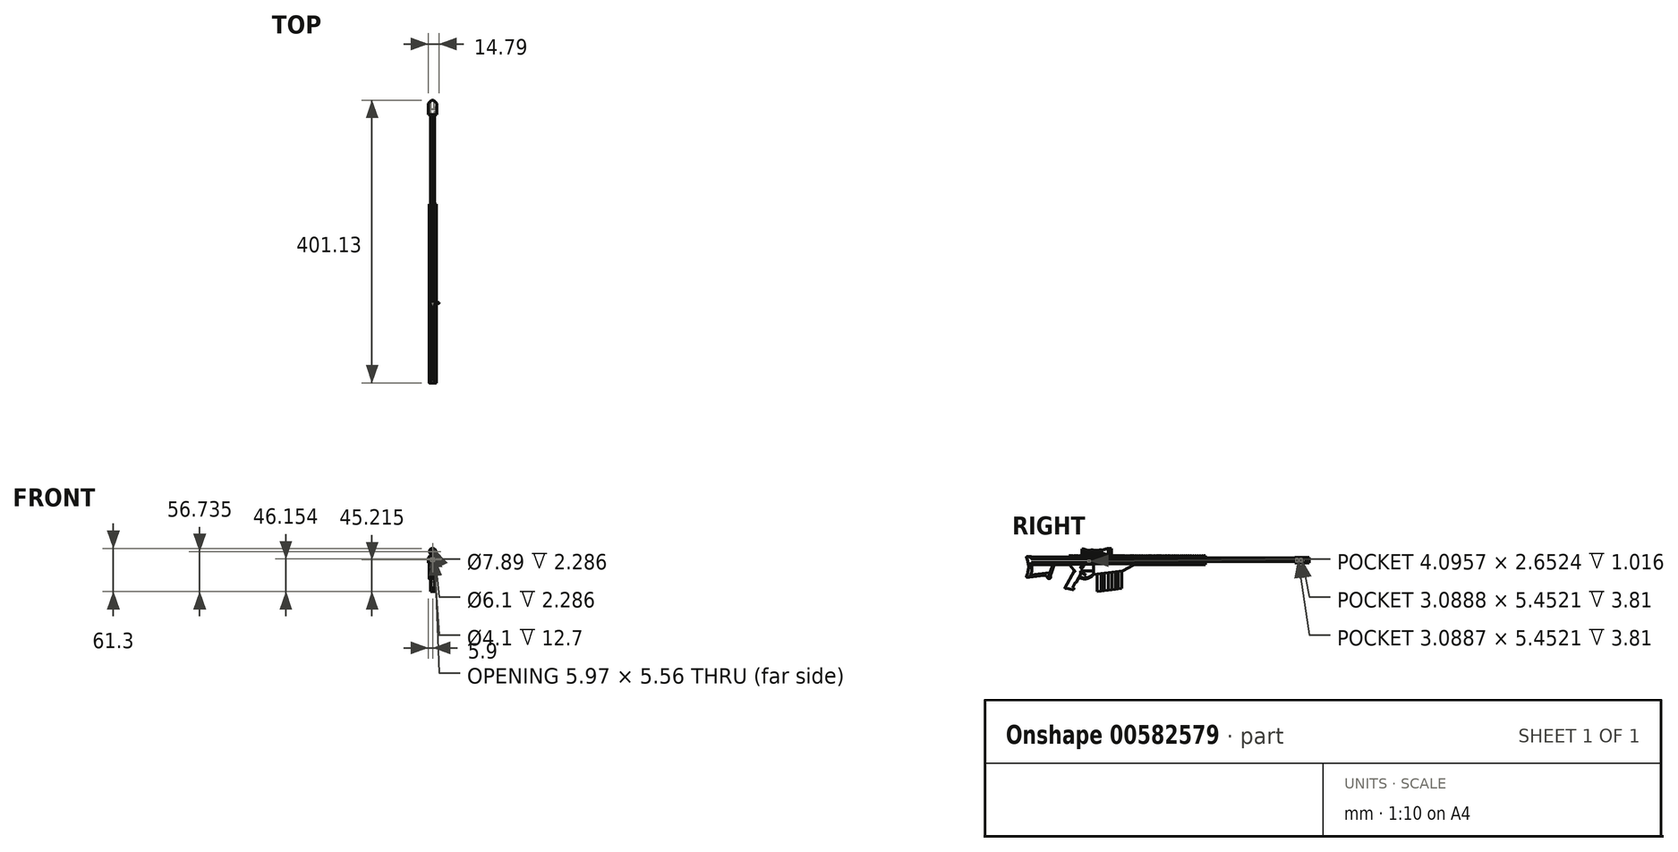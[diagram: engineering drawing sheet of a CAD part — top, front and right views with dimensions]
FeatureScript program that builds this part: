
annotation { "Feature Type Name" : "Feature", "Feature Type Description" : "" }
export const myFeature = defineFeature(function(context is Context, id is Id, definition is map)
    precondition{}
    {
        {
            var Q0;
            Q0=qCreatedBy(makeId("Right.planeOp"),FACE);
            var sketch = newSketch(context, id + "F0", { "sketchPlane" : qUnion([Q0])});
            skArc(sketch, "E0", {"start": v(-85.12, 1.27) * mm, "mid": v(-82.19, 14.92) * mm, "end": v(-85.15, 28.57) * mm});
            skLineSegment(sketch, "E1", {"start": v(-84.31, 0.17) * mm, "end": v(-60.4, 3.1) * mm});
            skArc(sketch, "E2", {"start": v(-55.44, 0) * mm, "mid": v(-57.37, 2.43) * mm, "end": v(-60.4, 3.1) * mm});
            skArc(sketch, "E3", {"start": v(-55.44, 0) * mm, "mid": v(-51.74, -1.3) * mm, "end": v(-51.3, 2.6) * mm});
            skLineSegment(sketch, "E4", {"start": v(-51.3, 2.6) * mm, "end": v(-45.62, 17.62) * mm});
            skArc(sketch, "E5", {"start": v(-80.7, 0.62) * mm, "mid": v(-77.5, 9.24) * mm, "end": v(-78, 18.43) * mm});
            skLineSegment(sketch, "E6", {"start": v(-47.77, 17.62) * mm, "end": v(-51.9, 6.68) * mm});
            skLineSegment(sketch, "E7", {"start": v(-51.9, 6.68) * mm, "end": v(-79.24, 3.33) * mm});
            skLineSegment(sketch, "E8", {"start": v(-83.48, 24.05) * mm, "end": v(66.86, 24.05) * mm});
            skLineSegment(sketch, "E9", {"start": v(-84.44, 29.67) * mm, "end": v(66.86, 29.67) * mm});
            skLineSegment(sketch, "E10", {"start": v(-78, 24.05) * mm, "end": v(-78, 29.67) * mm});
            skLineSegment(sketch, "E11", {"start": v(-45.62, 17.62) * mm, "end": v(66.86, 17.62) * mm});
            skLineSegment(sketch, "E12", {"start": v(-23.66, 17.62) * mm, "end": v(-17.13, 9.35) * mm});
            skLineSegment(sketch, "E13", {"start": v(-17.13, 9.35) * mm, "end": v(-30.74, -15.16) * mm});
            skLineSegment(sketch, "E14", {"start": v(-30.74, -15.16) * mm, "end": v(-19.23, -17.4) * mm});
            skLineSegment(sketch, "E15", {"start": v(-18.4, -17.02) * mm, "end": v(-17.74, -15.85) * mm});
            skLineSegment(sketch, "E16", {"start": v(-18.05, -14.79) * mm, "end": v(-18.83, -14.35) * mm});
            skLineSegment(sketch, "E17", {"start": v(-19.14, -13.29) * mm, "end": v(-15.75, -7.2) * mm});
            skLineSegment(sketch, "E18", {"start": v(-15.07, -6.8) * mm, "end": v(-13.98, -6.8) * mm});
            skLineSegment(sketch, "E19", {"start": v(-13.2, -6.01) * mm, "end": v(-13.2, -5.06) * mm});
            skLineSegment(sketch, "E20", {"start": v(-13.1, -4.68) * mm, "end": v(-10.5, 0) * mm});
            skPoint(sketch, "E21.visualSharp", {"position": v(-18.67, -17.52) * mm});
            skArc(sketch, "E21.filletArc", {"start": v(-19.23, -17.4) * mm, "mid": v(-18.75, -17.35) * mm, "end": v(-18.4, -17.02) * mm});
            skPoint(sketch, "E22.visualSharp", {"position": v(-17.36, -15.16) * mm});
            skArc(sketch, "E22.filletArc", {"start": v(-17.74, -15.85) * mm, "mid": v(-17.68, -15.25) * mm, "end": v(-18.05, -14.79) * mm});
            skPoint(sketch, "E23.visualSharp", {"position": v(-19.51, -13.97) * mm});
            skArc(sketch, "E23.filletArc", {"start": v(-19.14, -13.29) * mm, "mid": v(-19.2, -13.88) * mm, "end": v(-18.83, -14.35) * mm});
            skPoint(sketch, "E24.visualSharp", {"position": v(-15.53, -6.8) * mm});
            skArc(sketch, "E24.filletArc", {"start": v(-15.07, -6.8) * mm, "mid": v(-15.46, -6.9) * mm, "end": v(-15.75, -7.2) * mm});
            skPoint(sketch, "E25.visualSharp", {"position": v(-13.2, -6.8) * mm});
            skArc(sketch, "E25.filletArc", {"start": v(-13.98, -6.8) * mm, "mid": v(-13.43, -6.56) * mm, "end": v(-13.2, -6.01) * mm});
            skPoint(sketch, "E26.visualSharp", {"position": v(-13.2, -4.85) * mm});
            skArc(sketch, "E26.filletArc", {"start": v(-13.1, -4.68) * mm, "mid": v(-13.18, -4.86) * mm, "end": v(-13.2, -5.06) * mm});
            skLineSegment(sketch, "E27", {"start": v(-17.13, 9.35) * mm, "end": v(10.04, 9.35) * mm});
            skLineSegment(sketch, "E28", {"start": v(10.04, 9.35) * mm, "end": v(10.04, 17.62) * mm});
            skLineSegment(sketch, "E29", {"start": v(10.04, 9.35) * mm, "end": v(10.04, 4.02) * mm});
            skLineSegment(sketch, "E30", {"start": v(10.04, 4.02) * mm, "end": v(51.48, 9.35) * mm});
            skLineSegment(sketch, "E31", {"start": v(51.48, 9.35) * mm, "end": v(66.86, 17.62) * mm});
            skLineSegment(sketch, "E32", {"start": v(-10.5, 0) * mm, "end": v(-8.1, 4.34) * mm});
            skLineSegment(sketch, "E33", {"start": v(-8.1, 4.34) * mm, "end": v(-8.1, 9.35) * mm});
            skArc(sketch, "E34", {"start": v(-10.5, 0) * mm, "mid": v(0.48, -1.63) * mm, "end": v(10.04, 4.02) * mm});
            skArc(sketch, "E35", {"start": v(-9.92, 1.05) * mm, "mid": v(0.8, -0.43) * mm, "end": v(10.04, 5.2) * mm});
            skLineSegment(sketch, "E36", {"start": v(15.52, 4.72) * mm, "end": v(15.52, -19.95) * mm});
            skLineSegment(sketch, "E37", {"start": v(15.52, -19.95) * mm, "end": v(49.91, -15.53) * mm});
            skLineSegment(sketch, "E38", {"start": v(49.91, -15.53) * mm, "end": v(49.91, 9.15) * mm});
            skLineSegment(sketch, "E39", {"start": v(-78, 18.43) * mm, "end": v(-47.77, 17.62) * mm});
            skLineSegment(sketch, "E40", {"start": v(-45.62, 17.62) * mm, "end": v(-47.77, 17.62) * mm});
            skLineSegment(sketch, "E41", {"start": v(66.86, 24.05) * mm, "end": v(168.59, 24.05) * mm});
            skLineSegment(sketch, "E42", {"start": v(66.86, 29.67) * mm, "end": v(168.59, 29.67) * mm});
            skLineSegment(sketch, "E43", {"start": v(66.86, 17.62) * mm, "end": v(168.59, 17.62) * mm});
            skPoint(sketch, "E44.visualSharp", {"position": v(-85.68, 29.67) * mm});
            skArc(sketch, "E44.filletArc", {"start": v(-84.44, 29.67) * mm, "mid": v(-85.1, 29.31) * mm, "end": v(-85.15, 28.57) * mm});
            skPoint(sketch, "E45.visualSharp", {"position": v(-85.73, 0) * mm});
            skArc(sketch, "E45.filletArc", {"start": v(-85.12, 1.27) * mm, "mid": v(-85.04, 0.49) * mm, "end": v(-84.31, 0.17) * mm});
            skLineSegment(sketch, "E46", {"start": v(168.59, 29.67) * mm, "end": v(168.59, 24.05) * mm});
            skLineSegment(sketch, "E47", {"start": v(168.59, 17.62) * mm, "end": v(168.59, 24.05) * mm});
            skLineSegment(sketch, "E48", {"start": v(-78, 18.43) * mm, "end": v(-78, 24.05) * mm});
            skLineSegment(sketch, "E49", {"start": v(-45.62, 17.62) * mm, "end": v(-45.62, 18.57) * mm});
            skLineSegment(sketch, "E50", {"start": v(-45.62, 18.57) * mm, "end": v(-47.77, 18.57) * mm});
            skLineSegment(sketch, "E51", {"start": v(-47.77, 18.57) * mm, "end": v(-47.77, 17.62) * mm});
            skLineSegment(sketch, "E52", {"start": v(-23.66, 17.62) * mm, "end": v(-23.66, 19.53) * mm});
            skLineSegment(sketch, "E53", {"start": v(-23.66, 19.53) * mm, "end": v(66.86, 19.53) * mm});
            skLineSegment(sketch, "E54", {"start": v(66.86, 19.53) * mm, "end": v(66.86, 17.62) * mm});
            skLineSegment(sketch, "E55", {"start": v(10.04, 17.62) * mm, "end": v(10.04, 19.53) * mm});
            skLineSegment(sketch, "E56", {"start": v(20.6, -19.3) * mm, "end": v(20.6, 5.37) * mm});
            skLineSegment(sketch, "E57", {"start": v(25.68, 6.03) * mm, "end": v(25.68, -18.64) * mm});
            skLineSegment(sketch, "E58", {"start": v(30.76, 6.68) * mm, "end": v(30.76, -18) * mm});
            skLineSegment(sketch, "E59", {"start": v(35.84, 7.34) * mm, "end": v(35.84, -17.34) * mm});
            skLineSegment(sketch, "E60", {"start": v(40.92, 7.99) * mm, "end": v(40.92, -16.68) * mm});
            skLineSegment(sketch, "E61", {"start": v(45.24, 8.54) * mm, "end": v(45.24, -16.13) * mm});
            skSolve(sketch);
        }
        {
            var Q0;
            {var subQ1=sQuery(id+"F0.wireOp",EDGE,"E10");Q0=makeQuery(id+"F0.imprint","IMPRINT",FACE,{"disambiguationData":[TD([[makeQuery(id+"F0.imprint","IMPRINT",EDGE,{"derivedFrom":subQ1}),-1.0]])]});}
            var Q1;
            Q1=sQuery(id+"F0.wireOp",EDGE,"E8");
            revolve(context, id + "F1", {"entities" : qUnion([Q0]), "axis" : qUnion([Q1]), "revolveType" : RevolveType.FULL});
        }
        {
            var Q0;
            {var subQ0=sQuery(id+"F0.wireOp",EDGE,"E10");Q0=makeQuery(id+"F0.imprint","IMPRINT",FACE,{"disambiguationData":[TD([[makeQuery(id+"F0.imprint","IMPRINT",EDGE,{"derivedFrom":subQ0}),1.0]])]});}
            var Q1;
            {var subQ5=sQuery(id+"F0.wireOp",EDGE,"E45.filletArc");Q1=makeQuery(id+"F0.imprint","IMPRINT",FACE,{"disambiguationData":[TD([[makeQuery(id+"F0.imprint","IMPRINT",EDGE,{"derivedFrom":subQ5}),1.0]])]});}
            var Q2;
            {var subQ0=sQuery(id+"F0.wireOp",EDGE,"E2");Q2=makeQuery(id+"F0.imprint","IMPRINT",FACE,{"disambiguationData":[TD([[makeQuery(id+"F0.imprint","IMPRINT",EDGE,{"derivedFrom":subQ0}),-1.0]])]});}
            var Q3;
            Q3=makeQuery(id+"F0.imprint","IMPRINT",FACE,{"disambiguationData":[TD([[makeQuery(id+"F0.imprint","IMPRINT",EDGE,{"derivedFrom":sQuery(id+"F0.wireOp",EDGE,"E40")}),-1.0]])]});
            extrude(context, id + "F2", {"entities" : qUnion([Q0, Q1, Q2, Q3]), "operationType" : NewBodyOperationType.ADD, "endBound" : BoundingType.SYMMETRIC, "depth" : 10.16 * mm, "offsetDistance" : 25.4 * mm});
        }
        {
            var Q0;
            {var subQ0=sQuery(id+"F0.wireOp",EDGE,"E9");var subQ1=sQuery(id+"F0.wireOp",EDGE,"E48");var subQ2=sQuery(id+"F0.wireOp",EDGE,"E10");Q0=makeQuery(id+"F2.boolean.opBoolean","SPLIT",EDGE,{"disambiguationData":[TD([makeQuery(id+"F2.opExtrude","CAP_FACE",FACE,{"disambiguationData":[OSD([sQuery(id+"F0.wireOp",EDGE,"E0"),sQuery(id+"F0.wireOp",EDGE,"E1"),sQuery(id+"F0.wireOp",EDGE,"E2"),sQuery(id+"F0.wireOp",EDGE,"E3"),sQuery(id+"F0.wireOp",EDGE,"E4"),sQuery(id+"F0.wireOp",EDGE,"E5"),sQuery(id+"F0.wireOp",EDGE,"E6"),sQuery(id+"F0.wireOp",EDGE,"E7"),subQ0,subQ2,sQuery(id+"F0.wireOp",EDGE,"E44.filletArc"),sQuery(id+"F0.wireOp",EDGE,"E45.filletArc"),subQ1,sQuery(id+"F0.wireOp",EDGE,"E49"),sQuery(id+"F0.wireOp",EDGE,"E50"),sQuery(id+"F0.wireOp",EDGE,"E51")])],"isStart":true})])],"derivedFrom":makeQuery(id+"F2.opExtrude","SWEPT_EDGE",EDGE,{"disambiguationData":[OSD([subQ0,subQ2])]})});}
            var Q1;
            Q1=makeQuery(id+"F2.opExtrude","CAP_EDGE",EDGE,{"disambiguationData":[OSD([sQuery(id+"F0.wireOp",EDGE,"E7")])],"isStart":false});
            var Q2;
            Q2=makeQuery(id+"F2.opExtrude","CAP_EDGE",EDGE,{"disambiguationData":[OSD([sQuery(id+"F0.wireOp",EDGE,"E7")])],"isStart":true});
            fillet(context, id + "F3", {"entities" : qUnion([Q0, Q1, Q2]), "radius" : 5.08 * mm, "tangentPropagation" : true, "allowEdgeOverflow" : false});
        }
        {
            var Q0;
            {var subQ0=sQuery(id+"F0.wireOp",EDGE,"E9");var subQ1=makeQuery(id+"F1.opRevolve","SWEPT_FACE",FACE,{"disambiguationData":[OSD([subQ0,sQuery(id+"F0.wireOp",EDGE,"E42")])]});var subQ2=sQuery(id+"F0.wireOp",EDGE,"E10");var subQ3=makeQuery(id+"F1.opRevolve","SWEPT_FACE",FACE,{"disambiguationData":[OSD([subQ2])]});var subQ4=sQuery(id+"F0.wireOp",EDGE,"E48");Q0=makeQuery(id+"F2.boolean.opBoolean","SPLIT",EDGE,{"disambiguationData":[topologyDisambiguationEdgeConnected([subQ1,subQ3]),TD([makeQuery(id+"F2.opExtrude","CAP_FACE",FACE,{"disambiguationData":[OSD([sQuery(id+"F0.wireOp",EDGE,"E0"),sQuery(id+"F0.wireOp",EDGE,"E1"),sQuery(id+"F0.wireOp",EDGE,"E2"),sQuery(id+"F0.wireOp",EDGE,"E3"),sQuery(id+"F0.wireOp",EDGE,"E4"),sQuery(id+"F0.wireOp",EDGE,"E5"),sQuery(id+"F0.wireOp",EDGE,"E6"),sQuery(id+"F0.wireOp",EDGE,"E7"),subQ0,subQ2,sQuery(id+"F0.wireOp",EDGE,"E44.filletArc"),sQuery(id+"F0.wireOp",EDGE,"E45.filletArc"),subQ4,sQuery(id+"F0.wireOp",EDGE,"E49"),sQuery(id+"F0.wireOp",EDGE,"E50"),sQuery(id+"F0.wireOp",EDGE,"E51")])],"isStart":true})])],"derivedFrom":makeQuery(id+"F1.opRevolve","SWEPT_EDGE",EDGE,{"disambiguationData":[OSD([subQ0,subQ2])]})});}
            var Q1;
            {var subQ0=sQuery(id+"F0.wireOp",EDGE,"E9");var subQ1=makeQuery(id+"F1.opRevolve","SWEPT_FACE",FACE,{"disambiguationData":[OSD([subQ0,sQuery(id+"F0.wireOp",EDGE,"E42")])]});var subQ2=sQuery(id+"F0.wireOp",EDGE,"E10");var subQ3=makeQuery(id+"F1.opRevolve","SWEPT_FACE",FACE,{"disambiguationData":[OSD([subQ2])]});var subQ4=sQuery(id+"F0.wireOp",EDGE,"E48");Q1=makeQuery(id+"F2.boolean.opBoolean","SPLIT",EDGE,{"disambiguationData":[topologyDisambiguationEdgeConnected([subQ1,subQ3]),TD([makeQuery(id+"F2.opExtrude","CAP_FACE",FACE,{"disambiguationData":[OSD([sQuery(id+"F0.wireOp",EDGE,"E0"),sQuery(id+"F0.wireOp",EDGE,"E1"),sQuery(id+"F0.wireOp",EDGE,"E2"),sQuery(id+"F0.wireOp",EDGE,"E3"),sQuery(id+"F0.wireOp",EDGE,"E4"),sQuery(id+"F0.wireOp",EDGE,"E5"),sQuery(id+"F0.wireOp",EDGE,"E6"),sQuery(id+"F0.wireOp",EDGE,"E7"),subQ0,subQ2,sQuery(id+"F0.wireOp",EDGE,"E44.filletArc"),sQuery(id+"F0.wireOp",EDGE,"E45.filletArc"),subQ4,sQuery(id+"F0.wireOp",EDGE,"E49"),sQuery(id+"F0.wireOp",EDGE,"E50"),sQuery(id+"F0.wireOp",EDGE,"E51")])],"isStart":false})])],"derivedFrom":makeQuery(id+"F1.opRevolve","SWEPT_EDGE",EDGE,{"disambiguationData":[OSD([subQ0,subQ2])]})});}
            chamfer(context, id + "F4", {"entities" : qUnion([Q0, Q1]), "width" : 5.08 * mm, "tangentPropagation" : true});
        }
        {
            var Q0;
            Q0=makeQuery(id+"F2.opExtrude","CAP_EDGE",EDGE,{"disambiguationData":[OSD([sQuery(id+"F0.wireOp",EDGE,"E50")])],"isStart":false});
            var Q1;
            Q1=makeQuery(id+"F2.opExtrude","CAP_EDGE",EDGE,{"disambiguationData":[OSD([sQuery(id+"F0.wireOp",EDGE,"E50")])],"isStart":true});
            chamfer(context, id + "F5", {"entities" : qUnion([Q0, Q1]), "width" : 2.54 * mm, "tangentPropagation" : true});
        }
        {
            var Q0;
            Q0=makeQuery(id+"F2.opExtrude","SWEPT_EDGE",EDGE,{"disambiguationData":[OSD([sQuery(id+"F0.wireOp",EDGE,"E3"),sQuery(id+"F0.wireOp",EDGE,"E4")])]});
            fillet(context, id + "F6", {"entities" : qUnion([Q0]), "radius" : 5.08 * mm, "tangentPropagation" : true, "allowEdgeOverflow" : false});
        }
        {
            var Q0;
            {var subQ0=sQuery(id+"F0.wireOp",EDGE,"E52");Q0=makeQuery(id+"F0.imprint","IMPRINT",FACE,{"disambiguationData":[TD([[makeQuery(id+"F0.imprint","IMPRINT",EDGE,{"derivedFrom":subQ0}),-1.0]])]});}
            var Q1;
            {var subQ3=sQuery(id+"F0.wireOp",EDGE,"E12");Q1=makeQuery(id+"F0.imprint","IMPRINT",FACE,{"disambiguationData":[TD([[makeQuery(id+"F0.imprint","IMPRINT",EDGE,{"derivedFrom":subQ3}),1.0]])]});}
            var Q2;
            {var subQ1=sQuery(id+"F0.wireOp",EDGE,"E13");Q2=makeQuery(id+"F0.imprint","IMPRINT",FACE,{"disambiguationData":[TD([[makeQuery(id+"F0.imprint","IMPRINT",EDGE,{"derivedFrom":subQ1}),1.0]])]});}
            extrude(context, id + "F7", {"entities" : qUnion([Q0, Q1, Q2]), "operationType" : NewBodyOperationType.ADD, "endBound" : BoundingType.SYMMETRIC, "depth" : 5.08 * mm, "offsetDistance" : 25.4 * mm});
        }
        {
            var Q0;
            Q0=makeQuery(id+"F7.opExtrude","CAP_EDGE",EDGE,{"disambiguationData":[OSD([sQuery(id+"F0.wireOp",EDGE,"E13")])],"isStart":true});
            var Q1;
            Q1=makeQuery(id+"F7.opExtrude","CAP_EDGE",EDGE,{"disambiguationData":[OSD([sQuery(id+"F0.wireOp",EDGE,"E13")])],"isStart":false});
            fillet(context, id + "F8", {"entities" : qUnion([Q0, Q1]), "radius" : 2.3 * mm, "tangentPropagation" : true, "allowEdgeOverflow" : false});
        }
        {
            var Q0;
            Q0=makeQuery(id+"F7.opExtrude","CAP_EDGE",EDGE,{"disambiguationData":[OSD([sQuery(id+"F0.wireOp",EDGE,"E20"),sQuery(id+"F0.wireOp",EDGE,"E32")])],"isStart":false});
            var Q1;
            Q1=makeQuery(id+"F7.opExtrude","CAP_EDGE",EDGE,{"disambiguationData":[OSD([sQuery(id+"F0.wireOp",EDGE,"E17")])],"isStart":false});
            fillet(context, id + "F9", {"entities" : qUnion([Q0, Q1]), "radius" : 0.5 * mm, "tangentPropagation" : true, "allowEdgeOverflow" : false});
        }
        {
            var Q0;
            {var subQ0=sQuery(id+"F0.wireOp",EDGE,"E34");Q0=makeQuery(id+"F0.imprint","IMPRINT",FACE,{"disambiguationData":[TD([[makeQuery(id+"F0.imprint","IMPRINT",EDGE,{"derivedFrom":subQ0}),1.0]])]});}
            extrude(context, id + "F10", {"entities" : qUnion([Q0]), "operationType" : NewBodyOperationType.ADD, "endBound" : BoundingType.SYMMETRIC, "depth" : 1.27 * mm, "offsetDistance" : 25.4 * mm});
        }
        {
            var Q0;
            {var subQ1=sQuery(id+"F0.wireOp",EDGE,"E28");Q0=makeQuery(id+"F0.imprint","IMPRINT",FACE,{"disambiguationData":[TD([[makeQuery(id+"F0.imprint","IMPRINT",EDGE,{"derivedFrom":subQ1}),-1.0]])]});}
            var Q1;
            {var subQ0=sQuery(id+"F0.wireOp",EDGE,"E54");Q1=makeQuery(id+"F0.imprint","IMPRINT",FACE,{"disambiguationData":[TD([[makeQuery(id+"F0.imprint","IMPRINT",EDGE,{"derivedFrom":subQ0}),-1.0]])]});}
            extrude(context, id + "F11", {"entities" : qUnion([Q0, Q1]), "operationType" : NewBodyOperationType.ADD, "endBound" : BoundingType.SYMMETRIC, "depth" : 8.9 * mm, "offsetDistance" : 25.4 * mm});
        }
        {
            var Q0;
            {var subQ0=sQuery(id+"F0.wireOp",EDGE,"E38");Q0=makeQuery(id+"F0.imprint","IMPRINT",FACE,{"disambiguationData":[TD([[makeQuery(id+"F0.imprint","IMPRINT",EDGE,{"derivedFrom":subQ0}),1.0]])]});}
            var Q1;
            {var subQ0=sQuery(id+"F0.wireOp",EDGE,"E59");Q1=makeQuery(id+"F0.imprint","IMPRINT",FACE,{"disambiguationData":[TD([[makeQuery(id+"F0.imprint","IMPRINT",EDGE,{"derivedFrom":subQ0}),1.0]])]});}
            var Q2;
            {var subQ0=sQuery(id+"F0.wireOp",EDGE,"E57");Q2=makeQuery(id+"F0.imprint","IMPRINT",FACE,{"disambiguationData":[TD([[makeQuery(id+"F0.imprint","IMPRINT",EDGE,{"derivedFrom":subQ0}),1.0]])]});}
            var Q3;
            {var subQ0=sQuery(id+"F0.wireOp",EDGE,"E36");Q3=makeQuery(id+"F0.imprint","IMPRINT",FACE,{"disambiguationData":[TD([[makeQuery(id+"F0.imprint","IMPRINT",EDGE,{"derivedFrom":subQ0}),1.0]])]});}
            extrude(context, id + "F12", {"entities" : qUnion([Q0, Q1, Q2, Q3]), "operationType" : NewBodyOperationType.ADD, "endBound" : BoundingType.SYMMETRIC, "depth" : 6.35 * mm, "offsetDistance" : 25.4 * mm});
        }
        {
            var Q0;
            {var subQ0=sQuery(id+"F0.wireOp",EDGE,"E60");Q0=makeQuery(id+"F0.imprint","IMPRINT",FACE,{"disambiguationData":[TD([[makeQuery(id+"F0.imprint","IMPRINT",EDGE,{"derivedFrom":subQ0}),1.0]])]});}
            var Q1;
            {var subQ0=sQuery(id+"F0.wireOp",EDGE,"E58");Q1=makeQuery(id+"F0.imprint","IMPRINT",FACE,{"disambiguationData":[TD([[makeQuery(id+"F0.imprint","IMPRINT",EDGE,{"derivedFrom":subQ0}),1.0]])]});}
            var Q2;
            {var subQ0=sQuery(id+"F0.wireOp",EDGE,"E56");Q2=makeQuery(id+"F0.imprint","IMPRINT",FACE,{"disambiguationData":[TD([[makeQuery(id+"F0.imprint","IMPRINT",EDGE,{"derivedFrom":subQ0}),-1.0]])]});}
            extrude(context, id + "F13", {"entities" : qUnion([Q0, Q1, Q2]), "operationType" : NewBodyOperationType.ADD, "endBound" : BoundingType.SYMMETRIC, "depth" : 4.57 * mm, "offsetDistance" : 25.4 * mm});
        }
        {
            var Q0;
            Q0=makeQuery(id+"F2.opExtrude","SWEPT_FACE",FACE,{"disambiguationData":[OSD([sQuery(id+"F0.wireOp",EDGE,"E9")])]});
            var sketch = newSketch(context, id + "F14", { "sketchPlane" : qUnion([Q0])});
            skLineSegment(sketch, "E62", {"start": v(-9.31, -78) * mm, "end": v(-9.31, 177.46) * mm});
            skLineSegment(sketch, "E63", {"start": v(8.57, -78) * mm, "end": v(8.57, 177.46) * mm});
            skLineSegment(sketch, "E64", {"start": v(8.57, 177.46) * mm, "end": v(-9.31, 177.46) * mm});
            skLineSegment(sketch, "E65", {"start": v(-9.31, -78) * mm, "end": v(8.57, -78) * mm});
            skSolve(sketch);
        }
        {
            var Q0;
            {var subQ22=sQuery(id+"F14.wireOp",EDGE,"E62");Q0=makeQuery(id+"F14.imprint","IMPRINT",FACE,{"disambiguationData":[TD([[makeQuery(id+"F14.imprint","IMPRINT",EDGE,{"derivedFrom":subQ22}),-1.0]])]});}
            extrude(context, id + "F15", {"entities" : qUnion([Q0]), "operationType" : NewBodyOperationType.REMOVE, "oppositeDirection" : true, "depth" : 0.5 * mm, "offsetDistance" : 25.4 * mm});
        }
        {
            var Q0;
            Q0=makeQuery(id+"F11.boolean.opBoolean","INTERSECT",EDGE,{"disambiguationData":[OD(1.0)],"derivedFrom":[makeQuery(id+"F1.opRevolve","SWEPT_FACE",FACE,{"disambiguationData":[OSD([sQuery(id+"F0.wireOp",EDGE,"E9"),sQuery(id+"F0.wireOp",EDGE,"E42")])]}),makeQuery(id+"F11.opExtrude","SWEPT_FACE",FACE,{"disambiguationData":[OSD([sQuery(id+"F0.wireOp",EDGE,"E53")])]})]});
            var Q1;
            Q1=makeQuery(id+"F11.boolean.opBoolean","INTERSECT",EDGE,{"disambiguationData":[OD(0.0)],"derivedFrom":[makeQuery(id+"F1.opRevolve","SWEPT_FACE",FACE,{"disambiguationData":[OSD([sQuery(id+"F0.wireOp",EDGE,"E9"),sQuery(id+"F0.wireOp",EDGE,"E42")])]}),makeQuery(id+"F11.opExtrude","SWEPT_FACE",FACE,{"disambiguationData":[OSD([sQuery(id+"F0.wireOp",EDGE,"E53")])]})]});
            fillet(context, id + "F16", {"entities" : qUnion([Q0, Q1]), "radius" : 5.08 * mm, "tangentPropagation" : true, "allowEdgeOverflow" : false});
        }
        {
            var Q0;
            Q0=makeQuery(id+"F7.opExtrude","CAP_FACE",FACE,{"disambiguationData":[OSD([sQuery(id+"F0.wireOp",EDGE,"E12"),sQuery(id+"F0.wireOp",EDGE,"E13"),sQuery(id+"F0.wireOp",EDGE,"E14"),sQuery(id+"F0.wireOp",EDGE,"E15"),sQuery(id+"F0.wireOp",EDGE,"E16"),sQuery(id+"F0.wireOp",EDGE,"E17"),sQuery(id+"F0.wireOp",EDGE,"E18"),sQuery(id+"F0.wireOp",EDGE,"E19"),sQuery(id+"F0.wireOp",EDGE,"E20"),sQuery(id+"F0.wireOp",EDGE,"E21.filletArc"),sQuery(id+"F0.wireOp",EDGE,"E22.filletArc"),sQuery(id+"F0.wireOp",EDGE,"E23.filletArc"),sQuery(id+"F0.wireOp",EDGE,"E24.filletArc"),sQuery(id+"F0.wireOp",EDGE,"E25.filletArc"),sQuery(id+"F0.wireOp",EDGE,"E26.filletArc"),sQuery(id+"F0.wireOp",EDGE,"E27"),sQuery(id+"F0.wireOp",EDGE,"E28"),sQuery(id+"F0.wireOp",EDGE,"E32"),sQuery(id+"F0.wireOp",EDGE,"E33"),sQuery(id+"F0.wireOp",EDGE,"E52"),sQuery(id+"F0.wireOp",EDGE,"E53"),sQuery(id+"F0.wireOp",EDGE,"E55")])],"isStart":false});
            var sketch = newSketch(context, id + "F17", { "sketchPlane" : qUnion([Q0])});
            skCircle(sketch, "E66", {"center": v(-6.74, 14.66) * mm, "radius": 1.38 * mm});
            skLineSegment(sketch, "E67", {"start": v(-7.2, 15.97) * mm, "end": v(-5.5, 16.28) * mm});
            skLineSegment(sketch, "E68", {"start": v(-4.73, 15.04) * mm, "end": v(-5.64, 13.83) * mm});
            skPoint(sketch, "E69.visualSharp", {"position": v(-3.54, 16.63) * mm});
            skArc(sketch, "E69.filletArc", {"start": v(-4.73, 15.04) * mm, "mid": v(-4.7, 15.92) * mm, "end": v(-5.5, 16.28) * mm});
            skLineSegment(sketch, "E70", {"start": v(-5.5, 16.28) * mm, "end": v(-4.62, 16.55) * mm});
            skLineSegment(sketch, "E71", {"start": v(-4.1, 15.67) * mm, "end": v(-4.73, 15.04) * mm});
            skPoint(sketch, "E72.visualSharp", {"position": v(-2.55, 17.18) * mm});
            skArc(sketch, "E72.filletArc", {"start": v(-4.1, 15.67) * mm, "mid": v(-4.01, 16.31) * mm, "end": v(-4.62, 16.55) * mm});
            skSolve(sketch);
        }
        {
            var Q0;
            {var subQ0=sQuery(id+"F17.wireOp",EDGE,"E67");var subQ1=sQuery(id+"F17.wireOp",EDGE,"E66");var subQ2=makeQuery(id+"F17.imprint","INTERSECT",VERTEX,{"disambiguationData":[OD(0.0)],"derivedFrom":[subQ1,subQ0]});Q0=makeQuery(id+"F17.imprint","IMPRINT",FACE,{"disambiguationData":[TD([[makeQuery(id+"F17.imprint","IMPRINT",EDGE,{"disambiguationData":[TD([[subQ2,-1.0]])],"derivedFrom":subQ1}),1.0]])]});}
            extrude(context, id + "F18", {"entities" : qUnion([Q0]), "operationType" : NewBodyOperationType.ADD, "depth" : 0.5 * mm, "offsetDistance" : 25.4 * mm});
        }
        {
            var Q0;
            {var subQ0=sQuery(id+"F17.wireOp",EDGE,"E68");Q0=makeQuery(id+"F17.imprint","IMPRINT",FACE,{"disambiguationData":[TD([[makeQuery(id+"F17.imprint","IMPRINT",EDGE,{"derivedFrom":subQ0}),-1.0]])]});}
            var Q1;
            Q1=makeQuery(id+"F17.imprint","IMPRINT",FACE,{"disambiguationData":[TD([[makeQuery(id+"F17.imprint","IMPRINT",EDGE,{"derivedFrom":sQuery(id+"F17.wireOp",EDGE,"E69.filletArc")}),-1.0]])]});
            extrude(context, id + "F19", {"entities" : qUnion([Q0, Q1]), "operationType" : NewBodyOperationType.ADD, "depth" : 0.25 * mm, "offsetDistance" : 25.4 * mm});
        }
        {
            var Q0;
            Q0=makeQuery(id+"F3.opFillet","SPLIT",FACE,{"disambiguationData":[OD(0.0)],"derivedFrom":makeQuery(id+"F2.opExtrude","CAP_FACE",FACE,{"disambiguationData":[OSD([sQuery(id+"F0.wireOp",EDGE,"E0"),sQuery(id+"F0.wireOp",EDGE,"E1"),sQuery(id+"F0.wireOp",EDGE,"E2"),sQuery(id+"F0.wireOp",EDGE,"E3"),sQuery(id+"F0.wireOp",EDGE,"E4"),sQuery(id+"F0.wireOp",EDGE,"E5"),sQuery(id+"F0.wireOp",EDGE,"E6"),sQuery(id+"F0.wireOp",EDGE,"E7"),sQuery(id+"F0.wireOp",EDGE,"E9"),sQuery(id+"F0.wireOp",EDGE,"E10"),sQuery(id+"F0.wireOp",EDGE,"E44.filletArc"),sQuery(id+"F0.wireOp",EDGE,"E45.filletArc"),sQuery(id+"F0.wireOp",EDGE,"E48"),sQuery(id+"F0.wireOp",EDGE,"E49"),sQuery(id+"F0.wireOp",EDGE,"E50"),sQuery(id+"F0.wireOp",EDGE,"E51")])],"isStart":false})});
            var sketch = newSketch(context, id + "F20", { "sketchPlane" : qUnion([Q0])});
            skLineSegment(sketch, "E73", {"start": v(-80.84, 28.7) * mm, "end": v(-80.84, 20.23) * mm});
            skLineSegment(sketch, "E74", {"start": v(-80.84, 20.23) * mm, "end": v(174.1, 20.23) * mm});
            skLineSegment(sketch, "E75", {"start": v(174.1, 20.23) * mm, "end": v(174.1, 28.7) * mm});
            skLineSegment(sketch, "E76", {"start": v(174.1, 28.7) * mm, "end": v(-80.84, 28.7) * mm});
            skSolve(sketch);
        }
        {
            var Q0;
            Q0 = qSketchRegion(id + "F20", true);
            extrude(context, id + "F21", {"entities" : qUnion([Q0]), "operationType" : NewBodyOperationType.REMOVE, "depth" : 1.27 * mm, "offsetDistance" : 25.4 * mm});
        }
        {
            var Q0;
            Q0=makeQuery(id+"F3.opFillet","SPLIT",FACE,{"disambiguationData":[OD(0.0)],"derivedFrom":makeQuery(id+"F2.opExtrude","CAP_FACE",FACE,{"disambiguationData":[OSD([sQuery(id+"F0.wireOp",EDGE,"E0"),sQuery(id+"F0.wireOp",EDGE,"E1"),sQuery(id+"F0.wireOp",EDGE,"E2"),sQuery(id+"F0.wireOp",EDGE,"E3"),sQuery(id+"F0.wireOp",EDGE,"E4"),sQuery(id+"F0.wireOp",EDGE,"E5"),sQuery(id+"F0.wireOp",EDGE,"E6"),sQuery(id+"F0.wireOp",EDGE,"E7"),sQuery(id+"F0.wireOp",EDGE,"E9"),sQuery(id+"F0.wireOp",EDGE,"E10"),sQuery(id+"F0.wireOp",EDGE,"E44.filletArc"),sQuery(id+"F0.wireOp",EDGE,"E45.filletArc"),sQuery(id+"F0.wireOp",EDGE,"E48"),sQuery(id+"F0.wireOp",EDGE,"E49"),sQuery(id+"F0.wireOp",EDGE,"E50"),sQuery(id+"F0.wireOp",EDGE,"E51")])],"isStart":true})});
            var sketch = newSketch(context, id + "F22", { "sketchPlane" : qUnion([Q0])});
            skLineSegment(sketch, "E77", {"start": v(80.5, 28.24) * mm, "end": v(80.5, 19.7) * mm});
            skLineSegment(sketch, "E78", {"start": v(80.5, 19.7) * mm, "end": v(-177.39, 19.7) * mm});
            skLineSegment(sketch, "E79", {"start": v(80.5, 28.24) * mm, "end": v(-177.39, 28.57) * mm});
            skLineSegment(sketch, "E80", {"start": v(-177.39, 28.57) * mm, "end": v(-177.39, 19.7) * mm});
            skSolve(sketch);
        }
        {
            var Q0;
            Q0 = qSketchRegion(id + "F22", true);
            extrude(context, id + "F23", {"entities" : qUnion([Q0]), "operationType" : NewBodyOperationType.REMOVE, "depth" : 1.27 * mm, "offsetDistance" : 25.4 * mm});
        }
        {
            var Q0;
            Q0=makeQuery(id+"F21.boolean.opBoolean","MERGE",FACE,{"derivedFrom":[makeQuery(id+"F3.opFillet","SPLIT",FACE,{"disambiguationData":[OD(0.0)],"derivedFrom":makeQuery(id+"F2.opExtrude","CAP_FACE",FACE,{"disambiguationData":[OSD([sQuery(id+"F0.wireOp",EDGE,"E0"),sQuery(id+"F0.wireOp",EDGE,"E1"),sQuery(id+"F0.wireOp",EDGE,"E2"),sQuery(id+"F0.wireOp",EDGE,"E3"),sQuery(id+"F0.wireOp",EDGE,"E4"),sQuery(id+"F0.wireOp",EDGE,"E5"),sQuery(id+"F0.wireOp",EDGE,"E6"),sQuery(id+"F0.wireOp",EDGE,"E7"),sQuery(id+"F0.wireOp",EDGE,"E9"),sQuery(id+"F0.wireOp",EDGE,"E10"),sQuery(id+"F0.wireOp",EDGE,"E44.filletArc"),sQuery(id+"F0.wireOp",EDGE,"E45.filletArc"),sQuery(id+"F0.wireOp",EDGE,"E48"),sQuery(id+"F0.wireOp",EDGE,"E49"),sQuery(id+"F0.wireOp",EDGE,"E50"),sQuery(id+"F0.wireOp",EDGE,"E51")])],"isStart":false})}),makeQuery(id+"F21.opExtrude","CAP_FACE",FACE,{"disambiguationData":[OSD([sQuery(id+"F20.wireOp",EDGE,"E73"),sQuery(id+"F20.wireOp",EDGE,"E74"),sQuery(id+"F20.wireOp",EDGE,"E75"),sQuery(id+"F20.wireOp",EDGE,"E76")])],"isStart":true})]});
            var sketch = newSketch(context, id + "F24", { "sketchPlane" : qUnion([Q0])});
            skLineSegment(sketch, "E81", {"start": v(30.03, 22.08) * mm, "end": v(30.03, 26.01) * mm});
            skLineSegment(sketch, "E82", {"start": v(30.03, 26.01) * mm, "end": v(10.02, 26.01) * mm});
            skLineSegment(sketch, "E83", {"start": v(10.02, 26.01) * mm, "end": v(1.83, 23.46) * mm});
            skLineSegment(sketch, "E84", {"start": v(30.03, 22.08) * mm, "end": v(1.83, 22.08) * mm});
            skLineSegment(sketch, "E85", {"start": v(1.83, 22.08) * mm, "end": v(1.83, 23.46) * mm});
            skLineSegment(sketch, "E86", {"start": v(5.92, 24.74) * mm, "end": v(5.92, 22.08) * mm});
            skCircle(sketch, "E87", {"center": v(27.98, 23.55) * mm, "radius": 0.7 * mm});
            skSolve(sketch);
        }
        {
            var Q0;
            {var subQ1=sQuery(id+"F24.wireOp",EDGE,"E81");Q0=makeQuery(id+"F24.imprint","IMPRINT",FACE,{"disambiguationData":[TD([[makeQuery(id+"F24.imprint","IMPRINT",EDGE,{"derivedFrom":subQ1}),1.0]])]});}
            extrude(context, id + "F25", {"entities" : qUnion([Q0]), "operationType" : NewBodyOperationType.REMOVE, "oppositeDirection" : true, "depth" : 0.25 * mm, "offsetDistance" : 25.4 * mm});
        }
        {
            var Q0;
            {var subQ0=sQuery(id+"F24.wireOp",EDGE,"E85");Q0=makeQuery(id+"F24.imprint","IMPRINT",FACE,{"disambiguationData":[TD([[makeQuery(id+"F24.imprint","IMPRINT",EDGE,{"derivedFrom":subQ0}),-1.0]])]});}
            extrude(context, id + "F26", {"entities" : qUnion([Q0]), "operationType" : NewBodyOperationType.REMOVE, "oppositeDirection" : true, "depth" : 1.27 * mm, "offsetDistance" : 25.4 * mm});
        }
        {
            var Q0;
            Q0=makeQuery(id+"F24.imprint","IMPRINT",FACE,{"disambiguationData":[TD([[makeQuery(id+"F24.imprint","IMPRINT",EDGE,{"derivedFrom":sQuery(id+"F24.wireOp",EDGE,"E87")}),1.0]])]});
            extrude(context, id + "F27", {"entities" : qUnion([Q0]), "operationType" : NewBodyOperationType.ADD, "depth" : 3.8 * mm, "offsetDistance" : 25.4 * mm});
        }
        {
            var Q0;
            Q0=makeQuery(id+"F15.boolean.opBoolean","COPY",FACE,{"derivedFrom":makeQuery(id+"F15.opExtrude","CAP_FACE",FACE,{"disambiguationData":[OSD([sQuery(id+"F14.wireOp",EDGE,"E62"),sQuery(id+"F14.wireOp",EDGE,"E63"),sQuery(id+"F14.wireOp",EDGE,"E64"),sQuery(id+"F14.wireOp",EDGE,"E65")])],"isStart":false})});
            var sketch = newSketch(context, id + "F28", { "sketchPlane" : qUnion([Q0])});
            skLineSegment(sketch, "E88", {"start": v(2.34, -24.54) * mm, "end": v(-2.34, -24.54) * mm});
            skLineSegment(sketch, "E89", {"start": v(-2.34, -24.54) * mm, "end": v(-2.34, 168.59) * mm});
            skLineSegment(sketch, "E90", {"start": v(-2.34, 168.59) * mm, "end": v(2.34, 168.59) * mm});
            skLineSegment(sketch, "E91", {"start": v(2.34, 168.59) * mm, "end": v(2.34, -24.54) * mm});
            skLineSegment(sketch, "E92", {"start": v(-2.34, -23.66) * mm, "end": v(2.34, -23.66) * mm});
            skLineSegment(sketch, "E93", {"start": v(-2.34, -22.78) * mm, "end": v(2.34, -22.78) * mm});
            skLineSegment(sketch, "E94", {"start": v(-2.34, -21.93) * mm, "end": v(2.34, -21.93) * mm});
            skLineSegment(sketch, "E95", {"start": v(2.34, -21.22) * mm, "end": v(-2.34, -21.22) * mm});
            skLineSegment(sketch, "E96", {"start": v(2.34, -20.5) * mm, "end": v(-2.34, -20.5) * mm});
            skLineSegment(sketch, "E97", {"start": v(2.34, -19.63) * mm, "end": v(-2.34, -19.63) * mm});
            skLineSegment(sketch, "E98", {"start": v(2.34, -18.83) * mm, "end": v(-2.34, -18.83) * mm});
            skLineSegment(sketch, "E99", {"start": v(2.34, -17.9) * mm, "end": v(-2.34, -17.9) * mm});
            skLineSegment(sketch, "E100", {"start": v(2.34, -17) * mm, "end": v(-2.34, -17) * mm});
            skLineSegment(sketch, "E101", {"start": v(2.34, -16.26) * mm, "end": v(-2.34, -16.26) * mm});
            skLineSegment(sketch, "E102", {"start": v(-2.34, -15.4) * mm, "end": v(2.34, -15.4) * mm});
            skLineSegment(sketch, "E103", {"start": v(2.34, -14.44) * mm, "end": v(-2.34, -14.44) * mm});
            skLineSegment(sketch, "E104", {"start": v(2.34, -13.63) * mm, "end": v(-2.34, -13.63) * mm});
            skLineSegment(sketch, "E105", {"start": v(2.34, -12.48) * mm, "end": v(-2.34, -12.48) * mm});
            skLineSegment(sketch, "E106", {"start": v(2.34, -11.41) * mm, "end": v(-2.34, -11.41) * mm});
            skLineSegment(sketch, "E107", {"start": v(2.34, -10.25) * mm, "end": v(-2.34, -10.25) * mm});
            skLineSegment(sketch, "E108", {"start": v(2.34, -9.17) * mm, "end": v(-2.34, -9.17) * mm});
            skLineSegment(sketch, "E109", {"start": v(2.34, -8.22) * mm, "end": v(-2.34, -8.22) * mm});
            skLineSegment(sketch, "E110", {"start": v(2.34, -7.3) * mm, "end": v(-2.34, -7.3) * mm});
            skLineSegment(sketch, "E111", {"start": v(2.34, -6.5) * mm, "end": v(-2.34, -6.5) * mm});
            skLineSegment(sketch, "E112", {"start": v(2.34, -5.58) * mm, "end": v(-2.34, -5.58) * mm});
            skLineSegment(sketch, "E113", {"start": v(2.34, -4.59) * mm, "end": v(-2.34, -4.59) * mm});
            skLineSegment(sketch, "E114", {"start": v(2.34, -3.76) * mm, "end": v(-2.34, -3.76) * mm});
            skLineSegment(sketch, "E115", {"start": v(2.34, -2.88) * mm, "end": v(-2.34, -2.88) * mm});
            skLineSegment(sketch, "E116", {"start": v(2.34, -1.93) * mm, "end": v(-2.34, -1.93) * mm});
            skLineSegment(sketch, "E117", {"start": v(2.34, -1.13) * mm, "end": v(-2.34, -1.13) * mm});
            skLineSegment(sketch, "E118", {"start": v(2.34, -0.4) * mm, "end": v(-2.34, -0.4) * mm});
            skLineSegment(sketch, "E119", {"start": v(2.34, 0.45) * mm, "end": v(-2.34, 0.45) * mm});
            skLineSegment(sketch, "E120", {"start": v(2.34, 1.4) * mm, "end": v(-2.34, 1.4) * mm});
            skLineSegment(sketch, "E121", {"start": v(2.34, 2.2) * mm, "end": v(-2.34, 2.2) * mm});
            skLineSegment(sketch, "E122", {"start": v(2.34, 3.17) * mm, "end": v(-2.34, 3.17) * mm});
            skLineSegment(sketch, "E123", {"start": v(2.34, 4.07) * mm, "end": v(-2.34, 4.07) * mm});
            skLineSegment(sketch, "E124", {"start": v(2.34, 4.83) * mm, "end": v(-2.34, 4.83) * mm});
            skLineSegment(sketch, "E125", {"start": v(-2.34, 5.59) * mm, "end": v(2.34, 5.59) * mm});
            skLineSegment(sketch, "E126", {"start": v(-2.34, 6.44) * mm, "end": v(2.34, 6.44) * mm});
            skLineSegment(sketch, "E127", {"start": v(-2.34, 7.32) * mm, "end": v(2.34, 7.32) * mm});
            skLineSegment(sketch, "E128", {"start": v(-2.34, 8.28) * mm, "end": v(2.34, 8.28) * mm});
            skLineSegment(sketch, "E129", {"start": v(-2.34, 9.19) * mm, "end": v(2.34, 9.19) * mm});
            skLineSegment(sketch, "E130", {"start": v(-2.34, 10.05) * mm, "end": v(2.34, 10.05) * mm});
            skLineSegment(sketch, "E131", {"start": v(-2.34, 10.9) * mm, "end": v(2.34, 10.9) * mm});
            skLineSegment(sketch, "E132", {"start": v(-2.34, 11.83) * mm, "end": v(2.34, 11.83) * mm});
            skLineSegment(sketch, "E133", {"start": v(-2.34, 12.94) * mm, "end": v(2.34, 12.94) * mm});
            skLineSegment(sketch, "E134", {"start": v(-2.34, 14) * mm, "end": v(2.34, 14) * mm});
            skLineSegment(sketch, "E135", {"start": v(-2.34, 15.03) * mm, "end": v(2.34, 15.03) * mm});
            skLineSegment(sketch, "E136", {"start": v(-2.34, 16.07) * mm, "end": v(2.34, 16.07) * mm});
            skLineSegment(sketch, "E137", {"start": v(-2.34, 16.95) * mm, "end": v(2.34, 16.95) * mm});
            skLineSegment(sketch, "E138", {"start": v(-2.34, 17.75) * mm, "end": v(2.34, 17.75) * mm});
            skLineSegment(sketch, "E139", {"start": v(-2.34, 18.66) * mm, "end": v(2.34, 18.66) * mm});
            skLineSegment(sketch, "E140", {"start": v(-2.34, 19.77) * mm, "end": v(2.34, 19.77) * mm});
            skLineSegment(sketch, "E141", {"start": v(-2.34, 20.75) * mm, "end": v(2.34, 20.75) * mm});
            skLineSegment(sketch, "E142", {"start": v(-2.34, 21.53) * mm, "end": v(2.34, 21.53) * mm});
            skLineSegment(sketch, "E143", {"start": v(-2.34, 22.41) * mm, "end": v(2.34, 22.41) * mm});
            skLineSegment(sketch, "E144", {"start": v(-2.34, 23.37) * mm, "end": v(2.34, 23.37) * mm});
            skLineSegment(sketch, "E145", {"start": v(-2.34, 24.4) * mm, "end": v(2.34, 24.4) * mm});
            skLineSegment(sketch, "E146", {"start": v(-2.34, 25.59) * mm, "end": v(2.34, 25.59) * mm});
            skLineSegment(sketch, "E147", {"start": v(-2.34, 26.72) * mm, "end": v(2.34, 26.72) * mm});
            skLineSegment(sketch, "E148", {"start": v(-2.34, 27.98) * mm, "end": v(2.34, 27.98) * mm});
            skLineSegment(sketch, "E149", {"start": v(-2.34, 28.8) * mm, "end": v(2.34, 28.8) * mm});
            skLineSegment(sketch, "E150", {"start": v(-2.34, 29.59) * mm, "end": v(2.34, 29.59) * mm});
            skLineSegment(sketch, "E151", {"start": v(-2.34, 30.56) * mm, "end": v(2.34, 30.56) * mm});
            skLineSegment(sketch, "E152", {"start": v(-2.34, 31.37) * mm, "end": v(2.34, 31.37) * mm});
            skLineSegment(sketch, "E153", {"start": v(-2.34, 32.32) * mm, "end": v(2.34, 32.32) * mm});
            skLineSegment(sketch, "E154", {"start": v(-2.34, 33.36) * mm, "end": v(2.34, 33.36) * mm});
            skLineSegment(sketch, "E155", {"start": v(-2.34, 34.16) * mm, "end": v(2.34, 34.16) * mm});
            skLineSegment(sketch, "E156", {"start": v(-2.34, 35.25) * mm, "end": v(2.34, 35.25) * mm});
            skLineSegment(sketch, "E157", {"start": v(-2.34, 36.18) * mm, "end": v(2.34, 36.18) * mm});
            skLineSegment(sketch, "E158", {"start": v(-2.34, 37) * mm, "end": v(2.34, 37) * mm});
            skLineSegment(sketch, "E159", {"start": v(-2.34, 37.86) * mm, "end": v(2.34, 37.86) * mm});
            skLineSegment(sketch, "E160", {"start": v(-2.34, 38.64) * mm, "end": v(2.34, 38.64) * mm});
            skLineSegment(sketch, "E161", {"start": v(-2.34, 39.6) * mm, "end": v(2.34, 39.6) * mm});
            skLineSegment(sketch, "E162", {"start": v(-2.34, 40.68) * mm, "end": v(2.34, 40.68) * mm});
            skLineSegment(sketch, "E163", {"start": v(-2.34, 41.54) * mm, "end": v(2.34, 41.54) * mm});
            skLineSegment(sketch, "E164", {"start": v(-2.34, 42.35) * mm, "end": v(2.34, 42.35) * mm});
            skLineSegment(sketch, "E165", {"start": v(-2.34, 43.31) * mm, "end": v(2.34, 43.31) * mm});
            skLineSegment(sketch, "E166", {"start": v(-2.34, 44.36) * mm, "end": v(2.34, 44.36) * mm});
            skLineSegment(sketch, "E167", {"start": v(-2.34, 45.08) * mm, "end": v(2.34, 45.08) * mm});
            skLineSegment(sketch, "E168", {"start": v(-2.34, 46.22) * mm, "end": v(2.34, 46.22) * mm});
            skLineSegment(sketch, "E169", {"start": v(-2.34, 46.94) * mm, "end": v(2.34, 46.94) * mm});
            skLineSegment(sketch, "E170", {"start": v(-2.34, 47.78) * mm, "end": v(2.34, 47.78) * mm});
            skLineSegment(sketch, "E171", {"start": v(-2.34, 48.52) * mm, "end": v(2.34, 48.52) * mm});
            skLineSegment(sketch, "E172", {"start": v(-2.34, 49.35) * mm, "end": v(2.34, 49.35) * mm});
            skLineSegment(sketch, "E173", {"start": v(-2.34, 50.22) * mm, "end": v(2.34, 50.22) * mm});
            skLineSegment(sketch, "E174", {"start": v(-2.34, 50.85) * mm, "end": v(2.34, 50.85) * mm});
            skLineSegment(sketch, "E175", {"start": v(-2.34, 51.7) * mm, "end": v(2.34, 51.7) * mm});
            skLineSegment(sketch, "E176", {"start": v(-2.34, 52.56) * mm, "end": v(2.34, 52.56) * mm});
            skLineSegment(sketch, "E177", {"start": v(-2.34, 53.55) * mm, "end": v(2.34, 53.55) * mm});
            skLineSegment(sketch, "E178", {"start": v(-2.34, 54.5) * mm, "end": v(2.34, 54.5) * mm});
            skLineSegment(sketch, "E179", {"start": v(-2.34, 55.59) * mm, "end": v(2.34, 55.59) * mm});
            skLineSegment(sketch, "E180", {"start": v(-2.34, 56.54) * mm, "end": v(2.34, 56.54) * mm});
            skLineSegment(sketch, "E181", {"start": v(-2.34, 57.6) * mm, "end": v(2.34, 57.6) * mm});
            skLineSegment(sketch, "E182", {"start": v(-2.34, 58.55) * mm, "end": v(2.34, 58.55) * mm});
            skLineSegment(sketch, "E183", {"start": v(-2.34, 59.57) * mm, "end": v(2.34, 59.57) * mm});
            skLineSegment(sketch, "E184", {"start": v(-2.34, 60.47) * mm, "end": v(2.34, 60.47) * mm});
            skLineSegment(sketch, "E185", {"start": v(-2.34, 61.46) * mm, "end": v(2.34, 61.46) * mm});
            skLineSegment(sketch, "E186", {"start": v(-2.34, 62.2) * mm, "end": v(2.34, 62.2) * mm});
            skLineSegment(sketch, "E187", {"start": v(-2.34, 63.06) * mm, "end": v(2.34, 63.06) * mm});
            skLineSegment(sketch, "E188", {"start": v(-2.34, 64.02) * mm, "end": v(2.34, 64.02) * mm});
            skLineSegment(sketch, "E189", {"start": v(-2.34, 64.78) * mm, "end": v(2.34, 64.78) * mm});
            skLineSegment(sketch, "E190", {"start": v(-2.34, 65.93) * mm, "end": v(2.34, 65.93) * mm});
            skLineSegment(sketch, "E191", {"start": v(-2.34, 66.8) * mm, "end": v(2.34, 66.8) * mm});
            skLineSegment(sketch, "E192", {"start": v(-2.34, 68) * mm, "end": v(2.34, 68) * mm});
            skLineSegment(sketch, "E193", {"start": v(-2.34, 69.45) * mm, "end": v(2.34, 69.45) * mm});
            skLineSegment(sketch, "E194", {"start": v(-2.34, 70.86) * mm, "end": v(2.34, 70.86) * mm});
            skLineSegment(sketch, "E195", {"start": v(2.34, 72.03) * mm, "end": v(-2.34, 72.03) * mm});
            skLineSegment(sketch, "E196", {"start": v(2.34, 73.63) * mm, "end": v(-2.34, 73.63) * mm});
            skLineSegment(sketch, "E197", {"start": v(2.34, 75.14) * mm, "end": v(-2.34, 75.14) * mm});
            skLineSegment(sketch, "E198", {"start": v(2.34, 76.6) * mm, "end": v(-2.34, 76.6) * mm});
            skLineSegment(sketch, "E199", {"start": v(2.38, 78.01) * mm, "end": v(-2.34, 78.01) * mm});
            skLineSegment(sketch, "E200", {"start": v(-2.34, 79.73) * mm, "end": v(2.34, 79.73) * mm});
            skLineSegment(sketch, "E201", {"start": v(2.34, 81.9) * mm, "end": v(-2.34, 81.9) * mm});
            skLineSegment(sketch, "E202", {"start": v(2.34, 82.88) * mm, "end": v(-2.34, 82.88) * mm});
            skLineSegment(sketch, "E203", {"start": v(-2.34, 84.02) * mm, "end": v(2.34, 84.02) * mm});
            skLineSegment(sketch, "E204", {"start": v(-2.34, 80.91) * mm, "end": v(2.34, 80.91) * mm});
            skLineSegment(sketch, "E205", {"start": v(-2.34, 85.14) * mm, "end": v(2.34, 85.14) * mm});
            skLineSegment(sketch, "E206", {"start": v(-2.34, 86.42) * mm, "end": v(2.34, 86.42) * mm});
            skLineSegment(sketch, "E207", {"start": v(2.34, 87.85) * mm, "end": v(-2.34, 87.85) * mm});
            skLineSegment(sketch, "E208", {"start": v(-2.34, 89.2) * mm, "end": v(2.34, 89.2) * mm});
            skLineSegment(sketch, "E209", {"start": v(2.34, 91.13) * mm, "end": v(-2.34, 91.13) * mm});
            skLineSegment(sketch, "E210", {"start": v(-2.34, 92.88) * mm, "end": v(2.34, 92.88) * mm});
            skLineSegment(sketch, "E211", {"start": v(-2.34, 94.59) * mm, "end": v(2.34, 94.59) * mm});
            skLineSegment(sketch, "E212", {"start": v(-2.34, 96.44) * mm, "end": v(2.34, 96.44) * mm});
            skLineSegment(sketch, "E213", {"start": v(-2.34, 98) * mm, "end": v(2.34, 98) * mm});
            skLineSegment(sketch, "E214", {"start": v(-2.34, 99.58) * mm, "end": v(2.34, 99.58) * mm});
            skLineSegment(sketch, "E215", {"start": v(-2.34, 101.43) * mm, "end": v(2.34, 101.43) * mm});
            skLineSegment(sketch, "E216", {"start": v(-2.34, 103.28) * mm, "end": v(2.34, 103.28) * mm});
            skLineSegment(sketch, "E217", {"start": v(-2.34, 105.13) * mm, "end": v(2.34, 105.13) * mm});
            skLineSegment(sketch, "E218", {"start": v(-2.34, 106.87) * mm, "end": v(2.34, 106.87) * mm});
            skLineSegment(sketch, "E219", {"start": v(-2.34, 108.48) * mm, "end": v(2.34, 108.48) * mm});
            skLineSegment(sketch, "E220", {"start": v(-2.34, 110.43) * mm, "end": v(2.34, 110.43) * mm});
            skLineSegment(sketch, "E221", {"start": v(-2.34, 112.3) * mm, "end": v(2.34, 112.3) * mm});
            skLineSegment(sketch, "E222", {"start": v(-2.34, 114.33) * mm, "end": v(2.34, 114.33) * mm});
            skLineSegment(sketch, "E223", {"start": v(-2.34, 116.53) * mm, "end": v(2.34, 116.53) * mm});
            skLineSegment(sketch, "E224", {"start": v(-2.34, 118.82) * mm, "end": v(2.34, 118.82) * mm});
            skLineSegment(sketch, "E225", {"start": v(-2.34, 117.74) * mm, "end": v(2.34, 117.74) * mm});
            skLineSegment(sketch, "E226", {"start": v(-2.34, 115.62) * mm, "end": v(2.34, 115.62) * mm});
            skLineSegment(sketch, "E227", {"start": v(-2.34, 113.2) * mm, "end": v(2.34, 113.2) * mm});
            skLineSegment(sketch, "E228", {"start": v(-2.34, 111.5) * mm, "end": v(2.34, 111.5) * mm});
            skLineSegment(sketch, "E229", {"start": v(-2.34, 109.68) * mm, "end": v(2.34, 109.68) * mm});
            skLineSegment(sketch, "E230", {"start": v(-2.34, 90.04) * mm, "end": v(2.34, 90.04) * mm});
            skLineSegment(sketch, "E231", {"start": v(-2.34, 91.95) * mm, "end": v(2.34, 91.95) * mm});
            skLineSegment(sketch, "E232", {"start": v(-2.34, 93.72) * mm, "end": v(2.34, 93.72) * mm});
            skLineSegment(sketch, "E233", {"start": v(-2.34, 95.55) * mm, "end": v(2.34, 95.55) * mm});
            skLineSegment(sketch, "E234", {"start": v(-2.34, 97.38) * mm, "end": v(2.34, 97.38) * mm});
            skLineSegment(sketch, "E235", {"start": v(-2.34, 98.79) * mm, "end": v(2.34, 98.79) * mm});
            skLineSegment(sketch, "E236", {"start": v(-2.34, 100.5) * mm, "end": v(2.34, 100.5) * mm});
            skLineSegment(sketch, "E237", {"start": v(-2.34, 102.38) * mm, "end": v(2.34, 102.38) * mm});
            skLineSegment(sketch, "E238", {"start": v(-2.34, 104.2) * mm, "end": v(2.34, 104.2) * mm});
            skLineSegment(sketch, "E239", {"start": v(-2.34, 105.91) * mm, "end": v(2.34, 105.91) * mm});
            skLineSegment(sketch, "E240", {"start": v(-2.34, 107.68) * mm, "end": v(2.34, 107.68) * mm});
            skLineSegment(sketch, "E241", {"start": v(-2.34, 119.77) * mm, "end": v(2.34, 119.77) * mm});
            skLineSegment(sketch, "E242", {"start": v(-2.34, 120.94) * mm, "end": v(2.34, 120.94) * mm});
            skLineSegment(sketch, "E243", {"start": v(-2.34, 122.04) * mm, "end": v(2.34, 122.04) * mm});
            skLineSegment(sketch, "E244", {"start": v(-2.34, 123.3) * mm, "end": v(2.34, 123.3) * mm});
            skLineSegment(sketch, "E245", {"start": v(-2.34, 124.7) * mm, "end": v(2.34, 124.7) * mm});
            skLineSegment(sketch, "E246", {"start": v(-2.34, 126.12) * mm, "end": v(2.34, 126.12) * mm});
            skLineSegment(sketch, "E247", {"start": v(-2.34, 127.4) * mm, "end": v(2.34, 127.4) * mm});
            skLineSegment(sketch, "E248", {"start": v(-2.34, 128.77) * mm, "end": v(2.34, 128.77) * mm});
            skLineSegment(sketch, "E249", {"start": v(-2.34, 130.27) * mm, "end": v(2.34, 130.27) * mm});
            skLineSegment(sketch, "E250", {"start": v(-2.34, 131.7) * mm, "end": v(2.34, 131.7) * mm});
            skLineSegment(sketch, "E251", {"start": v(-2.34, 133.26) * mm, "end": v(2.34, 133.26) * mm});
            skLineSegment(sketch, "E252", {"start": v(-2.34, 134.34) * mm, "end": v(2.34, 134.34) * mm});
            skLineSegment(sketch, "E253", {"start": v(-2.34, 135.84) * mm, "end": v(2.34, 135.84) * mm});
            skLineSegment(sketch, "E254", {"start": v(-2.34, 137.1) * mm, "end": v(2.34, 137.1) * mm});
            skLineSegment(sketch, "E255", {"start": v(-2.34, 138.54) * mm, "end": v(2.34, 138.54) * mm});
            skLineSegment(sketch, "E256", {"start": v(-2.34, 139.91) * mm, "end": v(2.34, 139.91) * mm});
            skLineSegment(sketch, "E257", {"start": v(-2.34, 141.2) * mm, "end": v(2.34, 141.2) * mm});
            skLineSegment(sketch, "E258", {"start": v(-2.34, 142.7) * mm, "end": v(2.34, 142.7) * mm});
            skLineSegment(sketch, "E259", {"start": v(-2.34, 144.26) * mm, "end": v(2.34, 144.26) * mm});
            skLineSegment(sketch, "E260", {"start": v(-2.34, 145.9) * mm, "end": v(2.34, 145.9) * mm});
            skLineSegment(sketch, "E261", {"start": v(-2.34, 147.47) * mm, "end": v(2.34, 147.47) * mm});
            skLineSegment(sketch, "E262", {"start": v(-2.34, 149.25) * mm, "end": v(2.34, 149.25) * mm});
            skLineSegment(sketch, "E263", {"start": v(-2.34, 151.24) * mm, "end": v(2.34, 151.24) * mm});
            skLineSegment(sketch, "E264", {"start": v(-2.34, 152.67) * mm, "end": v(2.34, 152.67) * mm});
            skLineSegment(sketch, "E265", {"start": v(-2.34, 154.3) * mm, "end": v(2.34, 154.3) * mm});
            skLineSegment(sketch, "E266", {"start": v(-2.34, 155.6) * mm, "end": v(2.34, 155.6) * mm});
            skLineSegment(sketch, "E267", {"start": v(-2.34, 157.16) * mm, "end": v(2.34, 157.16) * mm});
            skLineSegment(sketch, "E268", {"start": v(-2.34, 158.87) * mm, "end": v(2.34, 158.87) * mm});
            skLineSegment(sketch, "E269", {"start": v(-2.34, 160.44) * mm, "end": v(2.34, 160.44) * mm});
            skLineSegment(sketch, "E270", {"start": v(-2.34, 161.93) * mm, "end": v(2.34, 161.93) * mm});
            skLineSegment(sketch, "E271", {"start": v(-2.34, 163.71) * mm, "end": v(2.34, 163.71) * mm});
            skLineSegment(sketch, "E272", {"start": v(-2.34, 164.85) * mm, "end": v(2.34, 164.85) * mm});
            skLineSegment(sketch, "E273", {"start": v(-2.34, 166.28) * mm, "end": v(2.34, 166.28) * mm});
            skLineSegment(sketch, "E274", {"start": v(-2.34, 167.56) * mm, "end": v(2.34, 167.56) * mm});
            skSolve(sketch);
        }
        {
            var Q0;
            Q0 = qSketchRegion(id + "F28", true);
            extrude(context, id + "F29", {"entities" : qUnion([Q0]), "operationType" : NewBodyOperationType.ADD, "depth" : 1.27 * mm, "offsetDistance" : 25.4 * mm});
        }
        {
            var Q0;
            {var subQ0=sQuery(id+"F28.wireOp",EDGE,"E88");Q0=makeQuery(id+"F28.imprint","IMPRINT",FACE,{"disambiguationData":[TD([[makeQuery(id+"F28.imprint","IMPRINT",EDGE,{"derivedFrom":subQ0}),-1.0]])]});}
            var Q1;
            {var subQ0=sQuery(id+"F28.wireOp",EDGE,"E93");Q1=makeQuery(id+"F28.imprint","IMPRINT",FACE,{"disambiguationData":[TD([[makeQuery(id+"F28.imprint","IMPRINT",EDGE,{"derivedFrom":subQ0}),1.0]])]});}
            var Q2;
            {var subQ0=sQuery(id+"F28.wireOp",EDGE,"E95");Q2=makeQuery(id+"F28.imprint","IMPRINT",FACE,{"disambiguationData":[TD([[makeQuery(id+"F28.imprint","IMPRINT",EDGE,{"derivedFrom":subQ0}),-1.0]])]});}
            var Q3;
            {var subQ0=sQuery(id+"F28.wireOp",EDGE,"E97");Q3=makeQuery(id+"F28.imprint","IMPRINT",FACE,{"disambiguationData":[TD([[makeQuery(id+"F28.imprint","IMPRINT",EDGE,{"derivedFrom":subQ0}),-1.0]])]});}
            var Q4;
            {var subQ0=sQuery(id+"F28.wireOp",EDGE,"E99");Q4=makeQuery(id+"F28.imprint","IMPRINT",FACE,{"disambiguationData":[TD([[makeQuery(id+"F28.imprint","IMPRINT",EDGE,{"derivedFrom":subQ0}),-1.0]])]});}
            var Q5;
            {var subQ0=sQuery(id+"F28.wireOp",EDGE,"E101");Q5=makeQuery(id+"F28.imprint","IMPRINT",FACE,{"disambiguationData":[TD([[makeQuery(id+"F28.imprint","IMPRINT",EDGE,{"derivedFrom":subQ0}),-1.0]])]});}
            var Q6;
            {var subQ0=sQuery(id+"F28.wireOp",EDGE,"E103");Q6=makeQuery(id+"F28.imprint","IMPRINT",FACE,{"disambiguationData":[TD([[makeQuery(id+"F28.imprint","IMPRINT",EDGE,{"derivedFrom":subQ0}),-1.0]])]});}
            var Q7;
            {var subQ0=sQuery(id+"F28.wireOp",EDGE,"E105");Q7=makeQuery(id+"F28.imprint","IMPRINT",FACE,{"disambiguationData":[TD([[makeQuery(id+"F28.imprint","IMPRINT",EDGE,{"derivedFrom":subQ0}),-1.0]])]});}
            var Q8;
            {var subQ0=sQuery(id+"F28.wireOp",EDGE,"E107");Q8=makeQuery(id+"F28.imprint","IMPRINT",FACE,{"disambiguationData":[TD([[makeQuery(id+"F28.imprint","IMPRINT",EDGE,{"derivedFrom":subQ0}),-1.0]])]});}
            var Q9;
            {var subQ0=sQuery(id+"F28.wireOp",EDGE,"E109");Q9=makeQuery(id+"F28.imprint","IMPRINT",FACE,{"disambiguationData":[TD([[makeQuery(id+"F28.imprint","IMPRINT",EDGE,{"derivedFrom":subQ0}),-1.0]])]});}
            var Q10;
            {var subQ0=sQuery(id+"F28.wireOp",EDGE,"E111");Q10=makeQuery(id+"F28.imprint","IMPRINT",FACE,{"disambiguationData":[TD([[makeQuery(id+"F28.imprint","IMPRINT",EDGE,{"derivedFrom":subQ0}),-1.0]])]});}
            var Q11;
            {var subQ0=sQuery(id+"F28.wireOp",EDGE,"E113");Q11=makeQuery(id+"F28.imprint","IMPRINT",FACE,{"disambiguationData":[TD([[makeQuery(id+"F28.imprint","IMPRINT",EDGE,{"derivedFrom":subQ0}),-1.0]])]});}
            var Q12;
            {var subQ0=sQuery(id+"F28.wireOp",EDGE,"E115");Q12=makeQuery(id+"F28.imprint","IMPRINT",FACE,{"disambiguationData":[TD([[makeQuery(id+"F28.imprint","IMPRINT",EDGE,{"derivedFrom":subQ0}),-1.0]])]});}
            var Q13;
            {var subQ0=sQuery(id+"F28.wireOp",EDGE,"E117");Q13=makeQuery(id+"F28.imprint","IMPRINT",FACE,{"disambiguationData":[TD([[makeQuery(id+"F28.imprint","IMPRINT",EDGE,{"derivedFrom":subQ0}),-1.0]])]});}
            var Q14;
            {var subQ0=sQuery(id+"F28.wireOp",EDGE,"E119");Q14=makeQuery(id+"F28.imprint","IMPRINT",FACE,{"disambiguationData":[TD([[makeQuery(id+"F28.imprint","IMPRINT",EDGE,{"derivedFrom":subQ0}),-1.0]])]});}
            var Q15;
            {var subQ0=sQuery(id+"F28.wireOp",EDGE,"E121");Q15=makeQuery(id+"F28.imprint","IMPRINT",FACE,{"disambiguationData":[TD([[makeQuery(id+"F28.imprint","IMPRINT",EDGE,{"derivedFrom":subQ0}),-1.0]])]});}
            var Q16;
            {var subQ0=sQuery(id+"F28.wireOp",EDGE,"E123");Q16=makeQuery(id+"F28.imprint","IMPRINT",FACE,{"disambiguationData":[TD([[makeQuery(id+"F28.imprint","IMPRINT",EDGE,{"derivedFrom":subQ0}),-1.0]])]});}
            var Q17;
            {var subQ0=sQuery(id+"F28.wireOp",EDGE,"E125");Q17=makeQuery(id+"F28.imprint","IMPRINT",FACE,{"disambiguationData":[TD([[makeQuery(id+"F28.imprint","IMPRINT",EDGE,{"derivedFrom":subQ0}),1.0]])]});}
            var Q18;
            {var subQ0=sQuery(id+"F28.wireOp",EDGE,"E127");Q18=makeQuery(id+"F28.imprint","IMPRINT",FACE,{"disambiguationData":[TD([[makeQuery(id+"F28.imprint","IMPRINT",EDGE,{"derivedFrom":subQ0}),1.0]])]});}
            var Q19;
            {var subQ0=sQuery(id+"F28.wireOp",EDGE,"E129");Q19=makeQuery(id+"F28.imprint","IMPRINT",FACE,{"disambiguationData":[TD([[makeQuery(id+"F28.imprint","IMPRINT",EDGE,{"derivedFrom":subQ0}),1.0]])]});}
            var Q20;
            {var subQ0=sQuery(id+"F28.wireOp",EDGE,"E131");Q20=makeQuery(id+"F28.imprint","IMPRINT",FACE,{"disambiguationData":[TD([[makeQuery(id+"F28.imprint","IMPRINT",EDGE,{"derivedFrom":subQ0}),1.0]])]});}
            var Q21;
            {var subQ0=sQuery(id+"F28.wireOp",EDGE,"E133");Q21=makeQuery(id+"F28.imprint","IMPRINT",FACE,{"disambiguationData":[TD([[makeQuery(id+"F28.imprint","IMPRINT",EDGE,{"derivedFrom":subQ0}),1.0]])]});}
            var Q22;
            {var subQ0=sQuery(id+"F28.wireOp",EDGE,"E135");Q22=makeQuery(id+"F28.imprint","IMPRINT",FACE,{"disambiguationData":[TD([[makeQuery(id+"F28.imprint","IMPRINT",EDGE,{"derivedFrom":subQ0}),1.0]])]});}
            var Q23;
            {var subQ0=sQuery(id+"F28.wireOp",EDGE,"E137");Q23=makeQuery(id+"F28.imprint","IMPRINT",FACE,{"disambiguationData":[TD([[makeQuery(id+"F28.imprint","IMPRINT",EDGE,{"derivedFrom":subQ0}),1.0]])]});}
            var Q24;
            {var subQ0=sQuery(id+"F28.wireOp",EDGE,"E139");Q24=makeQuery(id+"F28.imprint","IMPRINT",FACE,{"disambiguationData":[TD([[makeQuery(id+"F28.imprint","IMPRINT",EDGE,{"derivedFrom":subQ0}),1.0]])]});}
            var Q25;
            {var subQ0=sQuery(id+"F28.wireOp",EDGE,"E141");Q25=makeQuery(id+"F28.imprint","IMPRINT",FACE,{"disambiguationData":[TD([[makeQuery(id+"F28.imprint","IMPRINT",EDGE,{"derivedFrom":subQ0}),1.0]])]});}
            var Q26;
            {var subQ0=sQuery(id+"F28.wireOp",EDGE,"E143");Q26=makeQuery(id+"F28.imprint","IMPRINT",FACE,{"disambiguationData":[TD([[makeQuery(id+"F28.imprint","IMPRINT",EDGE,{"derivedFrom":subQ0}),1.0]])]});}
            var Q27;
            {var subQ0=sQuery(id+"F28.wireOp",EDGE,"E145");Q27=makeQuery(id+"F28.imprint","IMPRINT",FACE,{"disambiguationData":[TD([[makeQuery(id+"F28.imprint","IMPRINT",EDGE,{"derivedFrom":subQ0}),1.0]])]});}
            var Q28;
            {var subQ0=sQuery(id+"F28.wireOp",EDGE,"E147");Q28=makeQuery(id+"F28.imprint","IMPRINT",FACE,{"disambiguationData":[TD([[makeQuery(id+"F28.imprint","IMPRINT",EDGE,{"derivedFrom":subQ0}),1.0]])]});}
            var Q29;
            {var subQ0=sQuery(id+"F28.wireOp",EDGE,"E149");Q29=makeQuery(id+"F28.imprint","IMPRINT",FACE,{"disambiguationData":[TD([[makeQuery(id+"F28.imprint","IMPRINT",EDGE,{"derivedFrom":subQ0}),1.0]])]});}
            var Q30;
            {var subQ0=sQuery(id+"F28.wireOp",EDGE,"E151");Q30=makeQuery(id+"F28.imprint","IMPRINT",FACE,{"disambiguationData":[TD([[makeQuery(id+"F28.imprint","IMPRINT",EDGE,{"derivedFrom":subQ0}),1.0]])]});}
            var Q31;
            {var subQ0=sQuery(id+"F28.wireOp",EDGE,"E153");Q31=makeQuery(id+"F28.imprint","IMPRINT",FACE,{"disambiguationData":[TD([[makeQuery(id+"F28.imprint","IMPRINT",EDGE,{"derivedFrom":subQ0}),1.0]])]});}
            var Q32;
            {var subQ0=sQuery(id+"F28.wireOp",EDGE,"E155");Q32=makeQuery(id+"F28.imprint","IMPRINT",FACE,{"disambiguationData":[TD([[makeQuery(id+"F28.imprint","IMPRINT",EDGE,{"derivedFrom":subQ0}),1.0]])]});}
            var Q33;
            {var subQ0=sQuery(id+"F28.wireOp",EDGE,"E157");Q33=makeQuery(id+"F28.imprint","IMPRINT",FACE,{"disambiguationData":[TD([[makeQuery(id+"F28.imprint","IMPRINT",EDGE,{"derivedFrom":subQ0}),1.0]])]});}
            var Q34;
            {var subQ0=sQuery(id+"F28.wireOp",EDGE,"E159");Q34=makeQuery(id+"F28.imprint","IMPRINT",FACE,{"disambiguationData":[TD([[makeQuery(id+"F28.imprint","IMPRINT",EDGE,{"derivedFrom":subQ0}),1.0]])]});}
            var Q35;
            {var subQ0=sQuery(id+"F28.wireOp",EDGE,"E161");Q35=makeQuery(id+"F28.imprint","IMPRINT",FACE,{"disambiguationData":[TD([[makeQuery(id+"F28.imprint","IMPRINT",EDGE,{"derivedFrom":subQ0}),1.0]])]});}
            var Q36;
            {var subQ0=sQuery(id+"F28.wireOp",EDGE,"E163");Q36=makeQuery(id+"F28.imprint","IMPRINT",FACE,{"disambiguationData":[TD([[makeQuery(id+"F28.imprint","IMPRINT",EDGE,{"derivedFrom":subQ0}),1.0]])]});}
            var Q37;
            {var subQ0=sQuery(id+"F28.wireOp",EDGE,"E165");Q37=makeQuery(id+"F28.imprint","IMPRINT",FACE,{"disambiguationData":[TD([[makeQuery(id+"F28.imprint","IMPRINT",EDGE,{"derivedFrom":subQ0}),1.0]])]});}
            var Q38;
            {var subQ0=sQuery(id+"F28.wireOp",EDGE,"E167");Q38=makeQuery(id+"F28.imprint","IMPRINT",FACE,{"disambiguationData":[TD([[makeQuery(id+"F28.imprint","IMPRINT",EDGE,{"derivedFrom":subQ0}),1.0]])]});}
            var Q39;
            {var subQ0=sQuery(id+"F28.wireOp",EDGE,"E169");Q39=makeQuery(id+"F28.imprint","IMPRINT",FACE,{"disambiguationData":[TD([[makeQuery(id+"F28.imprint","IMPRINT",EDGE,{"derivedFrom":subQ0}),1.0]])]});}
            var Q40;
            {var subQ0=sQuery(id+"F28.wireOp",EDGE,"E171");Q40=makeQuery(id+"F28.imprint","IMPRINT",FACE,{"disambiguationData":[TD([[makeQuery(id+"F28.imprint","IMPRINT",EDGE,{"derivedFrom":subQ0}),1.0]])]});}
            var Q41;
            {var subQ0=sQuery(id+"F28.wireOp",EDGE,"E173");Q41=makeQuery(id+"F28.imprint","IMPRINT",FACE,{"disambiguationData":[TD([[makeQuery(id+"F28.imprint","IMPRINT",EDGE,{"derivedFrom":subQ0}),1.0]])]});}
            var Q42;
            {var subQ0=sQuery(id+"F28.wireOp",EDGE,"E175");Q42=makeQuery(id+"F28.imprint","IMPRINT",FACE,{"disambiguationData":[TD([[makeQuery(id+"F28.imprint","IMPRINT",EDGE,{"derivedFrom":subQ0}),1.0]])]});}
            var Q43;
            {var subQ0=sQuery(id+"F28.wireOp",EDGE,"E177");Q43=makeQuery(id+"F28.imprint","IMPRINT",FACE,{"disambiguationData":[TD([[makeQuery(id+"F28.imprint","IMPRINT",EDGE,{"derivedFrom":subQ0}),1.0]])]});}
            var Q44;
            {var subQ0=sQuery(id+"F28.wireOp",EDGE,"E179");Q44=makeQuery(id+"F28.imprint","IMPRINT",FACE,{"disambiguationData":[TD([[makeQuery(id+"F28.imprint","IMPRINT",EDGE,{"derivedFrom":subQ0}),1.0]])]});}
            var Q45;
            {var subQ0=sQuery(id+"F28.wireOp",EDGE,"E181");Q45=makeQuery(id+"F28.imprint","IMPRINT",FACE,{"disambiguationData":[TD([[makeQuery(id+"F28.imprint","IMPRINT",EDGE,{"derivedFrom":subQ0}),1.0]])]});}
            var Q46;
            {var subQ0=sQuery(id+"F28.wireOp",EDGE,"E183");Q46=makeQuery(id+"F28.imprint","IMPRINT",FACE,{"disambiguationData":[TD([[makeQuery(id+"F28.imprint","IMPRINT",EDGE,{"derivedFrom":subQ0}),1.0]])]});}
            var Q47;
            {var subQ0=sQuery(id+"F28.wireOp",EDGE,"E185");Q47=makeQuery(id+"F28.imprint","IMPRINT",FACE,{"disambiguationData":[TD([[makeQuery(id+"F28.imprint","IMPRINT",EDGE,{"derivedFrom":subQ0}),1.0]])]});}
            var Q48;
            {var subQ0=sQuery(id+"F28.wireOp",EDGE,"E187");Q48=makeQuery(id+"F28.imprint","IMPRINT",FACE,{"disambiguationData":[TD([[makeQuery(id+"F28.imprint","IMPRINT",EDGE,{"derivedFrom":subQ0}),1.0]])]});}
            var Q49;
            {var subQ0=sQuery(id+"F28.wireOp",EDGE,"E189");Q49=makeQuery(id+"F28.imprint","IMPRINT",FACE,{"disambiguationData":[TD([[makeQuery(id+"F28.imprint","IMPRINT",EDGE,{"derivedFrom":subQ0}),1.0]])]});}
            var Q50;
            {var subQ0=sQuery(id+"F28.wireOp",EDGE,"E191");Q50=makeQuery(id+"F28.imprint","IMPRINT",FACE,{"disambiguationData":[TD([[makeQuery(id+"F28.imprint","IMPRINT",EDGE,{"derivedFrom":subQ0}),1.0]])]});}
            var Q51;
            {var subQ0=sQuery(id+"F28.wireOp",EDGE,"E193");Q51=makeQuery(id+"F28.imprint","IMPRINT",FACE,{"disambiguationData":[TD([[makeQuery(id+"F28.imprint","IMPRINT",EDGE,{"derivedFrom":subQ0}),1.0]])]});}
            var Q52;
            {var subQ0=sQuery(id+"F28.wireOp",EDGE,"E195");Q52=makeQuery(id+"F28.imprint","IMPRINT",FACE,{"disambiguationData":[TD([[makeQuery(id+"F28.imprint","IMPRINT",EDGE,{"derivedFrom":subQ0}),-1.0]])]});}
            var Q53;
            {var subQ0=sQuery(id+"F28.wireOp",EDGE,"E197");Q53=makeQuery(id+"F28.imprint","IMPRINT",FACE,{"disambiguationData":[TD([[makeQuery(id+"F28.imprint","IMPRINT",EDGE,{"derivedFrom":subQ0}),-1.0]])]});}
            var Q54;
            {var subQ3=sQuery(id+"F28.wireOp",EDGE,"E200");Q54=makeQuery(id+"F28.imprint","IMPRINT",FACE,{"disambiguationData":[TD([[makeQuery(id+"F28.imprint","IMPRINT",EDGE,{"derivedFrom":subQ3}),-1.0]])]});}
            var Q55;
            {var subQ0=sQuery(id+"F28.wireOp",EDGE,"E201");Q55=makeQuery(id+"F28.imprint","IMPRINT",FACE,{"disambiguationData":[TD([[makeQuery(id+"F28.imprint","IMPRINT",EDGE,{"derivedFrom":subQ0}),1.0]])]});}
            var Q56;
            {var subQ0=sQuery(id+"F28.wireOp",EDGE,"E202");Q56=makeQuery(id+"F28.imprint","IMPRINT",FACE,{"disambiguationData":[TD([[makeQuery(id+"F28.imprint","IMPRINT",EDGE,{"derivedFrom":subQ0}),-1.0]])]});}
            var Q57;
            {var subQ0=sQuery(id+"F28.wireOp",EDGE,"E205");Q57=makeQuery(id+"F28.imprint","IMPRINT",FACE,{"disambiguationData":[TD([[makeQuery(id+"F28.imprint","IMPRINT",EDGE,{"derivedFrom":subQ0}),1.0]])]});}
            var Q58;
            {var subQ0=sQuery(id+"F28.wireOp",EDGE,"E207");Q58=makeQuery(id+"F28.imprint","IMPRINT",FACE,{"disambiguationData":[TD([[makeQuery(id+"F28.imprint","IMPRINT",EDGE,{"derivedFrom":subQ0}),-1.0]])]});}
            var Q59;
            {var subQ0=sQuery(id+"F28.wireOp",EDGE,"E209");Q59=makeQuery(id+"F28.imprint","IMPRINT",FACE,{"disambiguationData":[TD([[makeQuery(id+"F28.imprint","IMPRINT",EDGE,{"derivedFrom":subQ0}),1.0]])]});}
            var Q60;
            {var subQ0=sQuery(id+"F28.wireOp",EDGE,"E210");Q60=makeQuery(id+"F28.imprint","IMPRINT",FACE,{"disambiguationData":[TD([[makeQuery(id+"F28.imprint","IMPRINT",EDGE,{"derivedFrom":subQ0}),-1.0]])]});}
            var Q61;
            {var subQ0=sQuery(id+"F28.wireOp",EDGE,"E211");Q61=makeQuery(id+"F28.imprint","IMPRINT",FACE,{"disambiguationData":[TD([[makeQuery(id+"F28.imprint","IMPRINT",EDGE,{"derivedFrom":subQ0}),-1.0]])]});}
            var Q62;
            {var subQ0=sQuery(id+"F28.wireOp",EDGE,"E212");Q62=makeQuery(id+"F28.imprint","IMPRINT",FACE,{"disambiguationData":[TD([[makeQuery(id+"F28.imprint","IMPRINT",EDGE,{"derivedFrom":subQ0}),-1.0]])]});}
            var Q63;
            {var subQ0=sQuery(id+"F28.wireOp",EDGE,"E213");Q63=makeQuery(id+"F28.imprint","IMPRINT",FACE,{"disambiguationData":[TD([[makeQuery(id+"F28.imprint","IMPRINT",EDGE,{"derivedFrom":subQ0}),-1.0]])]});}
            var Q64;
            {var subQ0=sQuery(id+"F28.wireOp",EDGE,"E214");Q64=makeQuery(id+"F28.imprint","IMPRINT",FACE,{"disambiguationData":[TD([[makeQuery(id+"F28.imprint","IMPRINT",EDGE,{"derivedFrom":subQ0}),-1.0]])]});}
            var Q65;
            {var subQ0=sQuery(id+"F28.wireOp",EDGE,"E215");Q65=makeQuery(id+"F28.imprint","IMPRINT",FACE,{"disambiguationData":[TD([[makeQuery(id+"F28.imprint","IMPRINT",EDGE,{"derivedFrom":subQ0}),-1.0]])]});}
            var Q66;
            {var subQ0=sQuery(id+"F28.wireOp",EDGE,"E216");Q66=makeQuery(id+"F28.imprint","IMPRINT",FACE,{"disambiguationData":[TD([[makeQuery(id+"F28.imprint","IMPRINT",EDGE,{"derivedFrom":subQ0}),-1.0]])]});}
            var Q67;
            {var subQ0=sQuery(id+"F28.wireOp",EDGE,"E217");Q67=makeQuery(id+"F28.imprint","IMPRINT",FACE,{"disambiguationData":[TD([[makeQuery(id+"F28.imprint","IMPRINT",EDGE,{"derivedFrom":subQ0}),-1.0]])]});}
            var Q68;
            {var subQ0=sQuery(id+"F28.wireOp",EDGE,"E218");Q68=makeQuery(id+"F28.imprint","IMPRINT",FACE,{"disambiguationData":[TD([[makeQuery(id+"F28.imprint","IMPRINT",EDGE,{"derivedFrom":subQ0}),-1.0]])]});}
            var Q69;
            {var subQ0=sQuery(id+"F28.wireOp",EDGE,"E219");Q69=makeQuery(id+"F28.imprint","IMPRINT",FACE,{"disambiguationData":[TD([[makeQuery(id+"F28.imprint","IMPRINT",EDGE,{"derivedFrom":subQ0}),-1.0]])]});}
            var Q70;
            {var subQ0=sQuery(id+"F28.wireOp",EDGE,"E220");Q70=makeQuery(id+"F28.imprint","IMPRINT",FACE,{"disambiguationData":[TD([[makeQuery(id+"F28.imprint","IMPRINT",EDGE,{"derivedFrom":subQ0}),-1.0]])]});}
            var Q71;
            {var subQ0=sQuery(id+"F28.wireOp",EDGE,"E221");Q71=makeQuery(id+"F28.imprint","IMPRINT",FACE,{"disambiguationData":[TD([[makeQuery(id+"F28.imprint","IMPRINT",EDGE,{"derivedFrom":subQ0}),-1.0]])]});}
            var Q72;
            {var subQ0=sQuery(id+"F28.wireOp",EDGE,"E222");Q72=makeQuery(id+"F28.imprint","IMPRINT",FACE,{"disambiguationData":[TD([[makeQuery(id+"F28.imprint","IMPRINT",EDGE,{"derivedFrom":subQ0}),-1.0]])]});}
            var Q73;
            {var subQ0=sQuery(id+"F28.wireOp",EDGE,"E223");Q73=makeQuery(id+"F28.imprint","IMPRINT",FACE,{"disambiguationData":[TD([[makeQuery(id+"F28.imprint","IMPRINT",EDGE,{"derivedFrom":subQ0}),-1.0]])]});}
            var Q74;
            {var subQ0=sQuery(id+"F28.wireOp",EDGE,"E224");Q74=makeQuery(id+"F28.imprint","IMPRINT",FACE,{"disambiguationData":[TD([[makeQuery(id+"F28.imprint","IMPRINT",EDGE,{"derivedFrom":subQ0}),-1.0]])]});}
            var Q75;
            {var subQ0=sQuery(id+"F28.wireOp",EDGE,"E241");Q75=makeQuery(id+"F28.imprint","IMPRINT",FACE,{"disambiguationData":[TD([[makeQuery(id+"F28.imprint","IMPRINT",EDGE,{"derivedFrom":subQ0}),1.0]])]});}
            var Q76;
            {var subQ0=sQuery(id+"F28.wireOp",EDGE,"E243");Q76=makeQuery(id+"F28.imprint","IMPRINT",FACE,{"disambiguationData":[TD([[makeQuery(id+"F28.imprint","IMPRINT",EDGE,{"derivedFrom":subQ0}),1.0]])]});}
            var Q77;
            {var subQ0=sQuery(id+"F28.wireOp",EDGE,"E245");Q77=makeQuery(id+"F28.imprint","IMPRINT",FACE,{"disambiguationData":[TD([[makeQuery(id+"F28.imprint","IMPRINT",EDGE,{"derivedFrom":subQ0}),1.0]])]});}
            var Q78;
            {var subQ0=sQuery(id+"F28.wireOp",EDGE,"E247");Q78=makeQuery(id+"F28.imprint","IMPRINT",FACE,{"disambiguationData":[TD([[makeQuery(id+"F28.imprint","IMPRINT",EDGE,{"derivedFrom":subQ0}),1.0]])]});}
            var Q79;
            {var subQ0=sQuery(id+"F28.wireOp",EDGE,"E249");Q79=makeQuery(id+"F28.imprint","IMPRINT",FACE,{"disambiguationData":[TD([[makeQuery(id+"F28.imprint","IMPRINT",EDGE,{"derivedFrom":subQ0}),1.0]])]});}
            var Q80;
            {var subQ0=sQuery(id+"F28.wireOp",EDGE,"E251");Q80=makeQuery(id+"F28.imprint","IMPRINT",FACE,{"disambiguationData":[TD([[makeQuery(id+"F28.imprint","IMPRINT",EDGE,{"derivedFrom":subQ0}),1.0]])]});}
            var Q81;
            {var subQ0=sQuery(id+"F28.wireOp",EDGE,"E253");Q81=makeQuery(id+"F28.imprint","IMPRINT",FACE,{"disambiguationData":[TD([[makeQuery(id+"F28.imprint","IMPRINT",EDGE,{"derivedFrom":subQ0}),1.0]])]});}
            var Q82;
            {var subQ0=sQuery(id+"F28.wireOp",EDGE,"E255");Q82=makeQuery(id+"F28.imprint","IMPRINT",FACE,{"disambiguationData":[TD([[makeQuery(id+"F28.imprint","IMPRINT",EDGE,{"derivedFrom":subQ0}),1.0]])]});}
            var Q83;
            {var subQ0=sQuery(id+"F28.wireOp",EDGE,"E257");Q83=makeQuery(id+"F28.imprint","IMPRINT",FACE,{"disambiguationData":[TD([[makeQuery(id+"F28.imprint","IMPRINT",EDGE,{"derivedFrom":subQ0}),1.0]])]});}
            var Q84;
            {var subQ0=sQuery(id+"F28.wireOp",EDGE,"E259");Q84=makeQuery(id+"F28.imprint","IMPRINT",FACE,{"disambiguationData":[TD([[makeQuery(id+"F28.imprint","IMPRINT",EDGE,{"derivedFrom":subQ0}),1.0]])]});}
            var Q85;
            {var subQ0=sQuery(id+"F28.wireOp",EDGE,"E261");Q85=makeQuery(id+"F28.imprint","IMPRINT",FACE,{"disambiguationData":[TD([[makeQuery(id+"F28.imprint","IMPRINT",EDGE,{"derivedFrom":subQ0}),1.0]])]});}
            var Q86;
            {var subQ0=sQuery(id+"F28.wireOp",EDGE,"E263");Q86=makeQuery(id+"F28.imprint","IMPRINT",FACE,{"disambiguationData":[TD([[makeQuery(id+"F28.imprint","IMPRINT",EDGE,{"derivedFrom":subQ0}),1.0]])]});}
            var Q87;
            {var subQ0=sQuery(id+"F28.wireOp",EDGE,"E265");Q87=makeQuery(id+"F28.imprint","IMPRINT",FACE,{"disambiguationData":[TD([[makeQuery(id+"F28.imprint","IMPRINT",EDGE,{"derivedFrom":subQ0}),1.0]])]});}
            var Q88;
            {var subQ0=sQuery(id+"F28.wireOp",EDGE,"E267");Q88=makeQuery(id+"F28.imprint","IMPRINT",FACE,{"disambiguationData":[TD([[makeQuery(id+"F28.imprint","IMPRINT",EDGE,{"derivedFrom":subQ0}),1.0]])]});}
            var Q89;
            {var subQ0=sQuery(id+"F28.wireOp",EDGE,"E269");Q89=makeQuery(id+"F28.imprint","IMPRINT",FACE,{"disambiguationData":[TD([[makeQuery(id+"F28.imprint","IMPRINT",EDGE,{"derivedFrom":subQ0}),1.0]])]});}
            var Q90;
            {var subQ0=sQuery(id+"F28.wireOp",EDGE,"E271");Q90=makeQuery(id+"F28.imprint","IMPRINT",FACE,{"disambiguationData":[TD([[makeQuery(id+"F28.imprint","IMPRINT",EDGE,{"derivedFrom":subQ0}),1.0]])]});}
            var Q91;
            {var subQ0=sQuery(id+"F28.wireOp",EDGE,"E273");Q91=makeQuery(id+"F28.imprint","IMPRINT",FACE,{"disambiguationData":[TD([[makeQuery(id+"F28.imprint","IMPRINT",EDGE,{"derivedFrom":subQ0}),1.0]])]});}
            var Q92;
            {var subQ0=sQuery(id+"F28.wireOp",EDGE,"E90");Q92=makeQuery(id+"F28.imprint","IMPRINT",FACE,{"disambiguationData":[TD([[makeQuery(id+"F28.imprint","IMPRINT",EDGE,{"derivedFrom":subQ0}),-1.0]])]});}
            extrude(context, id + "F30", {"entities" : qUnion([Q0, Q1, Q2, Q3, Q4, Q5, Q6, Q7, Q8, Q9, Q10, Q11, Q12, Q13, Q14, Q15, Q16, Q17, Q18, Q19, Q20, Q21, Q22, Q23, Q24, Q25, Q26, Q27, Q28, Q29, Q30, Q31, Q32, Q33, Q34, Q35, Q36, Q37, Q38, Q39, Q40, Q41, Q42, Q43, Q44, Q45, Q46, Q47, Q48, Q49, Q50, Q51, Q52, Q53, Q54, Q55, Q56, Q57, Q58, Q59, Q60, Q61, Q62, Q63, Q64, Q65, Q66, Q67, Q68, Q69, Q70, Q71, Q72, Q73, Q74, Q75, Q76, Q77, Q78, Q79, Q80, Q81, Q82, Q83, Q84, Q85, Q86, Q87, Q88, Q89, Q90, Q91, Q92]), "operationType" : NewBodyOperationType.ADD, "depth" : 1.78 * mm, "offsetDistance" : 25.4 * mm});
        }
        {
            var Q0;
            {var subQ0=sQuery(id+"F28.wireOp",EDGE,"E126");Q0=makeQuery(id+"F28.imprint","IMPRINT",FACE,{"disambiguationData":[TD([[makeQuery(id+"F28.imprint","IMPRINT",EDGE,{"derivedFrom":subQ0}),1.0]])]});}
            var Q1;
            {var subQ0=sQuery(id+"F28.wireOp",EDGE,"E127");Q1=makeQuery(id+"F28.imprint","IMPRINT",FACE,{"disambiguationData":[TD([[makeQuery(id+"F28.imprint","IMPRINT",EDGE,{"derivedFrom":subQ0}),1.0]])]});}
            var Q2;
            {var subQ0=sQuery(id+"F28.wireOp",EDGE,"E128");Q2=makeQuery(id+"F28.imprint","IMPRINT",FACE,{"disambiguationData":[TD([[makeQuery(id+"F28.imprint","IMPRINT",EDGE,{"derivedFrom":subQ0}),1.0]])]});}
            var Q3;
            {var subQ0=sQuery(id+"F28.wireOp",EDGE,"E139");Q3=makeQuery(id+"F28.imprint","IMPRINT",FACE,{"disambiguationData":[TD([[makeQuery(id+"F28.imprint","IMPRINT",EDGE,{"derivedFrom":subQ0}),1.0]])]});}
            var Q4;
            {var subQ0=sQuery(id+"F28.wireOp",EDGE,"E140");Q4=makeQuery(id+"F28.imprint","IMPRINT",FACE,{"disambiguationData":[TD([[makeQuery(id+"F28.imprint","IMPRINT",EDGE,{"derivedFrom":subQ0}),1.0]])]});}
            var Q5;
            {var subQ0=sQuery(id+"F28.wireOp",EDGE,"E141");Q5=makeQuery(id+"F28.imprint","IMPRINT",FACE,{"disambiguationData":[TD([[makeQuery(id+"F28.imprint","IMPRINT",EDGE,{"derivedFrom":subQ0}),1.0]])]});}
            extrude(context, id + "F31", {"entities" : qUnion([Q0, Q1, Q2, Q3, Q4, Q5]), "operationType" : NewBodyOperationType.ADD, "depth" : 7.62 * mm, "offsetDistance" : 25.4 * mm});
        }
        {
            var Q0;
            Q0=qCreatedBy(makeId("Right.planeOp"),FACE);
            var sketch = newSketch(context, id + "F32", { "sketchPlane" : qUnion([Q0])});
            skLineSegment(sketch, "E275.0", {"start": v(7.92, 36.79) * mm, "end": v(9.19, 36.79) * mm});
            skPoint(sketch, "E276.0", {"position": v(7.71, 36.79) * mm});
            skLineSegment(sketch, "E277.0", {"start": v(6.44, 36.79) * mm, "end": v(7.71, 36.79) * mm});
            skPoint(sketch, "E278.0", {"position": v(7.82, 36.79) * mm});
            skLineSegment(sketch, "E279.0", {"start": v(7.92, 36.79) * mm, "end": v(7.71, 36.79) * mm});
            skLineSegment(sketch, "E280.0", {"start": v(7.71, 36.79) * mm, "end": v(7.71, 30.94) * mm});
            skLineSegment(sketch, "E281.0", {"start": v(18.66, 36.79) * mm, "end": v(19.93, 36.79) * mm});
            skLineSegment(sketch, "E282.0", {"start": v(20.26, 36.79) * mm, "end": v(21.53, 36.79) * mm});
            skLineSegment(sketch, "E283.0", {"start": v(20.26, 36.79) * mm, "end": v(19.93, 36.79) * mm});
            skLineSegment(sketch, "E284.0", {"start": v(6.44, 30.94) * mm, "end": v(6.44, 36.79) * mm});
            skLineSegment(sketch, "E285.0", {"start": v(9.19, 36.79) * mm, "end": v(9.19, 30.94) * mm});
            skLineSegment(sketch, "E286.0", {"start": v(18.66, 30.44) * mm, "end": v(18.66, 36.79) * mm});
            skLineSegment(sketch, "E287.0", {"start": v(21.53, 36.79) * mm, "end": v(21.53, 30.44) * mm});
            skLineSegment(sketch, "E288", {"start": v(6.44, 34.95) * mm, "end": v(2.31, 34.95) * mm});
            skLineSegment(sketch, "E289", {"start": v(2.31, 34.95) * mm, "end": v(1.06, 34.74) * mm});
            skLineSegment(sketch, "E290", {"start": v(6.44, 34.95) * mm, "end": v(21.53, 34.95) * mm});
            skLineSegment(sketch, "E291", {"start": v(35.4, 36.79) * mm, "end": v(-6.54, 36.79) * mm});
            skLineSegment(sketch, "E292", {"start": v(-6.54, 36.79) * mm, "end": v(-6.54, 34.09) * mm});
            skLineSegment(sketch, "E293", {"start": v(21.53, 34.95) * mm, "end": v(30.76, 32.22) * mm});
            skLineSegment(sketch, "E294", {"start": v(30.76, 32.22) * mm, "end": v(35.4, 32.22) * mm});
            skLineSegment(sketch, "E295", {"start": v(35.4, 32.22) * mm, "end": v(35.4, 36.79) * mm});
            skLineSegment(sketch, "E296", {"start": v(1.06, 34.74) * mm, "end": v(-3.33, 33.24) * mm});
            skLineSegment(sketch, "E297", {"start": v(-3.33, 33.24) * mm, "end": v(-6.54, 33.24) * mm});
            skLineSegment(sketch, "E298", {"start": v(-6.54, 33.24) * mm, "end": v(-6.54, 34.09) * mm});
            skLineSegment(sketch, "E299", {"start": v(14.43, 36.79) * mm, "end": v(14.43, 41.24) * mm});
            skLineSegment(sketch, "E300", {"start": v(14.43, 41.24) * mm, "end": v(14.98, 41.24) * mm});
            skLineSegment(sketch, "E301", {"start": v(14.98, 41.24) * mm, "end": v(14.98, 36.79) * mm});
            skSolve(sketch);
        }
        {
            var Q0;
            {var subQ1=sQuery(id+"F32.wireOp",EDGE,"E285.0");var subQ5=sQuery(id+"F32.wireOp",EDGE,"E291");var subQ8=makeQuery(id+"F32.imprint","INTERSECT",VERTEX,{"derivedFrom":[subQ1,subQ5]});Q0=makeQuery(id+"F32.imprint","IMPRINT",FACE,{"disambiguationData":[TD([[makeQuery(id+"F32.imprint","IMPRINT",EDGE,{"disambiguationData":[TD([[subQ8,-1.0]])],"derivedFrom":subQ1}),1.0]])]});}
            var Q1;
            {var subQ4=sQuery(id+"F32.wireOp",EDGE,"E288");Q1=makeQuery(id+"F32.imprint","IMPRINT",FACE,{"disambiguationData":[TD([[makeQuery(id+"F32.imprint","IMPRINT",EDGE,{"derivedFrom":subQ4}),-1.0]])]});}
            var Q2;
            {var subQ0=sQuery(id+"F32.wireOp",EDGE,"E293");Q2=makeQuery(id+"F32.imprint","IMPRINT",FACE,{"disambiguationData":[TD([[makeQuery(id+"F32.imprint","IMPRINT",EDGE,{"derivedFrom":subQ0}),1.0]])]});}
            var Q3;
            Q3=sQuery(id+"F32.wireOp",EDGE,"E291");
            revolve(context, id + "F33", {"operationType" : NewBodyOperationType.ADD, "entities" : qUnion([Q0, Q1, Q2]), "axis" : qUnion([Q3]), "revolveType" : RevolveType.FULL});
        }
        {
            var Q0;
            Q0=makeQuery(id+"F31.opExtrude","CAP_FACE",FACE,{"disambiguationData":[OSD([sQuery(id+"F28.wireOp",EDGE,"E89"),sQuery(id+"F28.wireOp",EDGE,"E91"),sQuery(id+"F28.wireOp",EDGE,"E126"),sQuery(id+"F28.wireOp",EDGE,"E129")])],"isStart":false});
            var Q1;
            Q1=makeQuery(id+"F31.opExtrude","CAP_FACE",FACE,{"disambiguationData":[OSD([sQuery(id+"F28.wireOp",EDGE,"E89"),sQuery(id+"F28.wireOp",EDGE,"E91"),sQuery(id+"F28.wireOp",EDGE,"E139"),sQuery(id+"F28.wireOp",EDGE,"E142")])],"isStart":false});
            extrude(context, id + "F34", {"entities" : qUnion([Q0, Q1]), "operationType" : NewBodyOperationType.ADD, "depth" : 2.54 * mm, "offsetDistance" : 25.4 * mm});
        }
        {
            var Q0;
            Q0=makeQuery(id+"F34.opExtrude","CAP_EDGE",EDGE,{"disambiguationData":[OSD([sQuery(id+"F28.wireOp",EDGE,"E126")])],"isStart":false});
            var Q1;
            Q1=makeQuery(id+"F34.opExtrude","CAP_EDGE",EDGE,{"disambiguationData":[OSD([sQuery(id+"F28.wireOp",EDGE,"E129")])],"isStart":false});
            var Q2;
            {var subQ0=sQuery(id+"F28.wireOp",EDGE,"E91");var subQ1=makeQuery(id+"F28.imprint","INTERSECT",VERTEX,{"derivedFrom":[subQ0,sQuery(id+"F28.wireOp",EDGE,"E127")]});var subQ2=makeQuery(id+"F28.imprint","INTERSECT",VERTEX,{"derivedFrom":[subQ0,sQuery(id+"F28.wireOp",EDGE,"E128")]});Q2=makeQuery(id+"F34.opExtrude","CAP_EDGE",EDGE,{"disambiguationData":[OSD([subQ0]),TDD([makeQuery(id+"F31.opExtrude","CAP_EDGE",EDGE,{"disambiguationData":[OSD([subQ0]),TDD([makeQuery(id+"F28.imprint","IMPRINT",EDGE,{"disambiguationData":[TD([[subQ2,1.0]])],"derivedFrom":subQ0}),makeQuery(id+"F28.imprint","IMPRINT",EDGE,{"disambiguationData":[TD([[subQ1,1.0]])],"derivedFrom":subQ0}),makeQuery(id+"F28.imprint","IMPRINT",EDGE,{"disambiguationData":[TD([[makeQuery(id+"F28.imprint","INTERSECT",VERTEX,{"derivedFrom":[subQ0,sQuery(id+"F28.wireOp",EDGE,"E126")]}),1.0]])],"derivedFrom":subQ0})])],"isStart":false})])],"isStart":false});}
            var Q3;
            {var subQ0=sQuery(id+"F28.wireOp",EDGE,"E89");var subQ1=makeQuery(id+"F28.imprint","INTERSECT",VERTEX,{"derivedFrom":[subQ0,sQuery(id+"F28.wireOp",EDGE,"E127")]});var subQ2=makeQuery(id+"F28.imprint","INTERSECT",VERTEX,{"derivedFrom":[subQ0,sQuery(id+"F28.wireOp",EDGE,"E128")]});Q3=makeQuery(id+"F34.opExtrude","CAP_EDGE",EDGE,{"disambiguationData":[OSD([subQ0]),TDD([makeQuery(id+"F31.opExtrude","CAP_EDGE",EDGE,{"disambiguationData":[OSD([subQ0]),TDD([makeQuery(id+"F28.imprint","IMPRINT",EDGE,{"disambiguationData":[TD([[subQ2,-1.0]])],"derivedFrom":subQ0}),makeQuery(id+"F28.imprint","IMPRINT",EDGE,{"disambiguationData":[TD([[subQ1,-1.0]])],"derivedFrom":subQ0}),makeQuery(id+"F28.imprint","IMPRINT",EDGE,{"disambiguationData":[TD([[makeQuery(id+"F28.imprint","INTERSECT",VERTEX,{"derivedFrom":[subQ0,sQuery(id+"F28.wireOp",EDGE,"E126")]}),-1.0]])],"derivedFrom":subQ0})])],"isStart":false})])],"isStart":false});}
            var Q4;
            {var subQ0=sQuery(id+"F28.wireOp",EDGE,"E91");var subQ1=makeQuery(id+"F28.imprint","INTERSECT",VERTEX,{"derivedFrom":[subQ0,sQuery(id+"F28.wireOp",EDGE,"E140")]});var subQ2=makeQuery(id+"F28.imprint","INTERSECT",VERTEX,{"derivedFrom":[subQ0,sQuery(id+"F28.wireOp",EDGE,"E141")]});Q4=makeQuery(id+"F34.opExtrude","CAP_EDGE",EDGE,{"disambiguationData":[OSD([subQ0]),TDD([makeQuery(id+"F31.opExtrude","CAP_EDGE",EDGE,{"disambiguationData":[OSD([subQ0]),TDD([makeQuery(id+"F28.imprint","IMPRINT",EDGE,{"disambiguationData":[TD([[subQ2,1.0]])],"derivedFrom":subQ0}),makeQuery(id+"F28.imprint","IMPRINT",EDGE,{"disambiguationData":[TD([[subQ1,1.0]])],"derivedFrom":subQ0}),makeQuery(id+"F28.imprint","IMPRINT",EDGE,{"disambiguationData":[TD([[makeQuery(id+"F28.imprint","INTERSECT",VERTEX,{"derivedFrom":[subQ0,sQuery(id+"F28.wireOp",EDGE,"E139")]}),1.0]])],"derivedFrom":subQ0})])],"isStart":false})])],"isStart":false});}
            var Q5;
            Q5=makeQuery(id+"F34.opExtrude","CAP_EDGE",EDGE,{"disambiguationData":[OSD([sQuery(id+"F28.wireOp",EDGE,"E142")])],"isStart":false});
            var Q6;
            {var subQ0=sQuery(id+"F28.wireOp",EDGE,"E89");var subQ1=makeQuery(id+"F28.imprint","INTERSECT",VERTEX,{"derivedFrom":[subQ0,sQuery(id+"F28.wireOp",EDGE,"E140")]});var subQ2=makeQuery(id+"F28.imprint","INTERSECT",VERTEX,{"derivedFrom":[subQ0,sQuery(id+"F28.wireOp",EDGE,"E141")]});Q6=makeQuery(id+"F34.opExtrude","CAP_EDGE",EDGE,{"disambiguationData":[OSD([subQ0]),TDD([makeQuery(id+"F31.opExtrude","CAP_EDGE",EDGE,{"disambiguationData":[OSD([subQ0]),TDD([makeQuery(id+"F28.imprint","IMPRINT",EDGE,{"disambiguationData":[TD([[subQ2,-1.0]])],"derivedFrom":subQ0}),makeQuery(id+"F28.imprint","IMPRINT",EDGE,{"disambiguationData":[TD([[subQ1,-1.0]])],"derivedFrom":subQ0}),makeQuery(id+"F28.imprint","IMPRINT",EDGE,{"disambiguationData":[TD([[makeQuery(id+"F28.imprint","INTERSECT",VERTEX,{"derivedFrom":[subQ0,sQuery(id+"F28.wireOp",EDGE,"E139")]}),-1.0]])],"derivedFrom":subQ0})])],"isStart":false})])],"isStart":false});}
            var Q7;
            Q7=makeQuery(id+"F34.opExtrude","CAP_EDGE",EDGE,{"disambiguationData":[OSD([sQuery(id+"F28.wireOp",EDGE,"E139")])],"isStart":false});
            fillet(context, id + "F35", {"entities" : qUnion([Q0, Q1, Q2, Q3, Q4, Q5, Q6, Q7]), "radius" : 0.5 * mm, "tangentPropagation" : true, "allowEdgeOverflow" : false});
        }
        {
            var Q0;
            {var subQ0=sQuery(id+"F28.wireOp",EDGE,"E126");var subQ1=sQuery(id+"F28.wireOp",EDGE,"E91");Q0=makeQuery(id+"F34.boolean.opBoolean","MERGE",EDGE,{"derivedFrom":[makeQuery(id+"F31.opExtrude","SWEPT_EDGE",EDGE,{"disambiguationData":[OSD([subQ1,subQ0])]}),makeQuery(id+"F34.opExtrude","SWEPT_EDGE",EDGE,{"disambiguationData":[OSD([subQ1,subQ0])]})]});}
            var Q1;
            {var subQ0=sQuery(id+"F28.wireOp",EDGE,"E129");var subQ1=sQuery(id+"F28.wireOp",EDGE,"E91");Q1=makeQuery(id+"F34.boolean.opBoolean","MERGE",EDGE,{"derivedFrom":[makeQuery(id+"F31.opExtrude","SWEPT_EDGE",EDGE,{"disambiguationData":[OSD([subQ1,subQ0])]}),makeQuery(id+"F34.opExtrude","SWEPT_EDGE",EDGE,{"disambiguationData":[OSD([subQ1,subQ0])]})]});}
            var Q2;
            {var subQ0=sQuery(id+"F28.wireOp",EDGE,"E126");var subQ1=sQuery(id+"F28.wireOp",EDGE,"E89");Q2=makeQuery(id+"F34.boolean.opBoolean","MERGE",EDGE,{"derivedFrom":[makeQuery(id+"F31.opExtrude","SWEPT_EDGE",EDGE,{"disambiguationData":[OSD([subQ1,subQ0])]}),makeQuery(id+"F34.opExtrude","SWEPT_EDGE",EDGE,{"disambiguationData":[OSD([subQ1,subQ0])]})]});}
            var Q3;
            {var subQ0=sQuery(id+"F28.wireOp",EDGE,"E129");var subQ1=sQuery(id+"F28.wireOp",EDGE,"E89");Q3=makeQuery(id+"F34.boolean.opBoolean","MERGE",EDGE,{"derivedFrom":[makeQuery(id+"F31.opExtrude","SWEPT_EDGE",EDGE,{"disambiguationData":[OSD([subQ1,subQ0])]}),makeQuery(id+"F34.opExtrude","SWEPT_EDGE",EDGE,{"disambiguationData":[OSD([subQ1,subQ0])]})]});}
            var Q4;
            {var subQ0=sQuery(id+"F28.wireOp",EDGE,"E139");var subQ1=sQuery(id+"F28.wireOp",EDGE,"E89");Q4=makeQuery(id+"F34.boolean.opBoolean","MERGE",EDGE,{"derivedFrom":[makeQuery(id+"F31.boolean.opBoolean","MERGE",EDGE,{"derivedFrom":[makeQuery(id+"F30.opExtrude","SWEPT_EDGE",EDGE,{"disambiguationData":[OSD([subQ1,subQ0])]}),makeQuery(id+"F31.opExtrude","SWEPT_EDGE",EDGE,{"disambiguationData":[OSD([subQ1,subQ0])]})]}),makeQuery(id+"F34.opExtrude","SWEPT_EDGE",EDGE,{"disambiguationData":[OSD([subQ1,subQ0])]})]});}
            var Q5;
            {var subQ0=sQuery(id+"F28.wireOp",EDGE,"E142");var subQ1=sQuery(id+"F28.wireOp",EDGE,"E89");Q5=makeQuery(id+"F34.boolean.opBoolean","MERGE",EDGE,{"derivedFrom":[makeQuery(id+"F31.boolean.opBoolean","MERGE",EDGE,{"derivedFrom":[makeQuery(id+"F30.opExtrude","SWEPT_EDGE",EDGE,{"disambiguationData":[OSD([subQ1,subQ0])]}),makeQuery(id+"F31.opExtrude","SWEPT_EDGE",EDGE,{"disambiguationData":[OSD([subQ1,subQ0])]})]}),makeQuery(id+"F34.opExtrude","SWEPT_EDGE",EDGE,{"disambiguationData":[OSD([subQ1,subQ0])]})]});}
            var Q6;
            {var subQ0=sQuery(id+"F28.wireOp",EDGE,"E142");var subQ1=sQuery(id+"F28.wireOp",EDGE,"E91");Q6=makeQuery(id+"F34.boolean.opBoolean","MERGE",EDGE,{"derivedFrom":[makeQuery(id+"F31.boolean.opBoolean","MERGE",EDGE,{"derivedFrom":[makeQuery(id+"F30.opExtrude","SWEPT_EDGE",EDGE,{"disambiguationData":[OSD([subQ1,subQ0])]}),makeQuery(id+"F31.opExtrude","SWEPT_EDGE",EDGE,{"disambiguationData":[OSD([subQ1,subQ0])]})]}),makeQuery(id+"F34.opExtrude","SWEPT_EDGE",EDGE,{"disambiguationData":[OSD([subQ1,subQ0])]})]});}
            var Q7;
            {var subQ0=sQuery(id+"F28.wireOp",EDGE,"E139");var subQ1=sQuery(id+"F28.wireOp",EDGE,"E91");Q7=makeQuery(id+"F34.boolean.opBoolean","MERGE",EDGE,{"derivedFrom":[makeQuery(id+"F31.boolean.opBoolean","MERGE",EDGE,{"derivedFrom":[makeQuery(id+"F30.opExtrude","SWEPT_EDGE",EDGE,{"disambiguationData":[OSD([subQ1,subQ0])]}),makeQuery(id+"F31.opExtrude","SWEPT_EDGE",EDGE,{"disambiguationData":[OSD([subQ1,subQ0])]})]}),makeQuery(id+"F34.opExtrude","SWEPT_EDGE",EDGE,{"disambiguationData":[OSD([subQ1,subQ0])]})]});}
            fillet(context, id + "F36", {"entities" : qUnion([Q0, Q1, Q2, Q3, Q4, Q5, Q6, Q7]), "radius" : 0.25 * mm, "tangentPropagation" : true, "allowEdgeOverflow" : false});
        }
        {
            var Q0;
            {var subQ0=sQuery(id+"F0.wireOp",EDGE,"E45.filletArc");var subQ1=sQuery(id+"F0.wireOp",EDGE,"E44.filletArc");var subQ2=sQuery(id+"F0.wireOp",EDGE,"E9");var subQ4=sQuery(id+"F0.wireOp",EDGE,"E48");var subQ5=sQuery(id+"F0.wireOp",EDGE,"E10");var subQ6=sQuery(id+"F0.wireOp",EDGE,"E5");var subQ7=sQuery(id+"F0.wireOp",EDGE,"E1");var subQ8=sQuery(id+"F0.wireOp",EDGE,"E0");var subQ9=makeQuery(id+"F2.opExtrude","CAP_FACE",FACE,{"disambiguationData":[OSD([subQ8,subQ7,sQuery(id+"F0.wireOp",EDGE,"E2"),sQuery(id+"F0.wireOp",EDGE,"E3"),sQuery(id+"F0.wireOp",EDGE,"E4"),subQ6,sQuery(id+"F0.wireOp",EDGE,"E6"),sQuery(id+"F0.wireOp",EDGE,"E7"),subQ2,subQ5,subQ1,subQ0,subQ4,sQuery(id+"F0.wireOp",EDGE,"E49"),sQuery(id+"F0.wireOp",EDGE,"E50"),sQuery(id+"F0.wireOp",EDGE,"E51")])],"isStart":false});Q0=makeQuery(id+"F25.boolean.opBoolean","SPLIT",FACE,{"disambiguationData":[TD([makeQuery(id+"F1.opRevolve","SWEPT_FACE",FACE,{"disambiguationData":[OSD([sQuery(id+"F0.wireOp",EDGE,"E46")])]})])],"derivedFrom":makeQuery(id+"F21.boolean.opBoolean","MERGE",FACE,{"derivedFrom":[makeQuery(id+"F3.opFillet","SPLIT",FACE,{"disambiguationData":[OD(0.0)],"derivedFrom":subQ9}),makeQuery(id+"F21.opExtrude","CAP_FACE",FACE,{"disambiguationData":[OSD([sQuery(id+"F20.wireOp",EDGE,"E73"),sQuery(id+"F20.wireOp",EDGE,"E74"),sQuery(id+"F20.wireOp",EDGE,"E75"),sQuery(id+"F20.wireOp",EDGE,"E76")])],"isStart":true})]})});}
            var sketch = newSketch(context, id + "F37", { "sketchPlane" : qUnion([Q0])});
            skArc(sketch, "E302", {"start": v(74.25, 23.95) * mm, "mid": v(73.56, 22.8) * mm, "end": v(74.25, 21.63) * mm});
            skLineSegment(sketch, "E303", {"start": v(74.25, 23.95) * mm, "end": v(76.45, 23.95) * mm});
            skLineSegment(sketch, "E304", {"start": v(74.25, 21.63) * mm, "end": v(76.45, 21.63) * mm});
            skArc(sketch, "E305", {"start": v(76.45, 21.63) * mm, "mid": v(77.18, 22.8) * mm, "end": v(76.45, 23.95) * mm});
            skArc(sketch, "E306", {"start": v(80.53, 23.9) * mm, "mid": v(79.84, 22.74) * mm, "end": v(80.53, 21.57) * mm});
            skLineSegment(sketch, "E307", {"start": v(80.53, 23.9) * mm, "end": v(82.72, 23.9) * mm});
            skLineSegment(sketch, "E308", {"start": v(80.53, 21.57) * mm, "end": v(82.72, 21.57) * mm});
            skArc(sketch, "E309", {"start": v(82.72, 21.57) * mm, "mid": v(83.45, 22.74) * mm, "end": v(82.72, 23.9) * mm});
            skArc(sketch, "E310", {"start": v(86.66, 23.84) * mm, "mid": v(85.97, 22.68) * mm, "end": v(86.66, 21.52) * mm});
            skLineSegment(sketch, "E311", {"start": v(86.66, 23.84) * mm, "end": v(88.86, 23.84) * mm});
            skLineSegment(sketch, "E312", {"start": v(86.66, 21.52) * mm, "end": v(88.86, 21.52) * mm});
            skArc(sketch, "E313", {"start": v(88.86, 21.52) * mm, "mid": v(89.59, 22.68) * mm, "end": v(88.86, 23.84) * mm});
            skArc(sketch, "E314", {"start": v(92.94, 23.78) * mm, "mid": v(92.25, 22.62) * mm, "end": v(92.94, 21.46) * mm});
            skLineSegment(sketch, "E315", {"start": v(92.94, 23.78) * mm, "end": v(95.14, 23.78) * mm});
            skLineSegment(sketch, "E316", {"start": v(92.94, 21.46) * mm, "end": v(95.14, 21.46) * mm});
            skArc(sketch, "E317", {"start": v(95.14, 21.46) * mm, "mid": v(95.86, 22.62) * mm, "end": v(95.14, 23.78) * mm});
            skArc(sketch, "E318", {"start": v(98.77, 23.84) * mm, "mid": v(98.08, 22.68) * mm, "end": v(98.77, 21.52) * mm});
            skLineSegment(sketch, "E319", {"start": v(98.77, 23.84) * mm, "end": v(100.97, 23.84) * mm});
            skLineSegment(sketch, "E320", {"start": v(98.77, 21.52) * mm, "end": v(100.97, 21.52) * mm});
            skArc(sketch, "E321", {"start": v(100.97, 21.52) * mm, "mid": v(101.7, 22.68) * mm, "end": v(100.97, 23.84) * mm});
            skArc(sketch, "E322", {"start": v(105.05, 23.78) * mm, "mid": v(104.35, 22.62) * mm, "end": v(105.05, 21.46) * mm});
            skLineSegment(sketch, "E323", {"start": v(105.05, 23.78) * mm, "end": v(107.24, 23.78) * mm});
            skLineSegment(sketch, "E324", {"start": v(105.05, 21.46) * mm, "end": v(107.24, 21.46) * mm});
            skArc(sketch, "E325", {"start": v(107.24, 21.46) * mm, "mid": v(107.97, 22.62) * mm, "end": v(107.24, 23.78) * mm});
            skArc(sketch, "E326", {"start": v(111.18, 23.72) * mm, "mid": v(110.5, 22.56) * mm, "end": v(111.18, 21.4) * mm});
            skLineSegment(sketch, "E327", {"start": v(111.18, 23.72) * mm, "end": v(113.38, 23.72) * mm});
            skLineSegment(sketch, "E328", {"start": v(111.18, 21.4) * mm, "end": v(113.38, 21.4) * mm});
            skArc(sketch, "E329", {"start": v(113.38, 21.4) * mm, "mid": v(114.1, 22.56) * mm, "end": v(113.38, 23.72) * mm});
            skArc(sketch, "E330", {"start": v(117.46, 23.67) * mm, "mid": v(116.77, 22.5) * mm, "end": v(117.46, 21.35) * mm});
            skLineSegment(sketch, "E331", {"start": v(117.46, 23.67) * mm, "end": v(119.65, 23.67) * mm});
            skLineSegment(sketch, "E332", {"start": v(117.46, 21.35) * mm, "end": v(119.65, 21.35) * mm});
            skArc(sketch, "E333", {"start": v(119.65, 21.35) * mm, "mid": v(120.38, 22.5) * mm, "end": v(119.65, 23.67) * mm});
            skArc(sketch, "E334", {"start": v(123.5, 23.78) * mm, "mid": v(122.8, 22.62) * mm, "end": v(123.5, 21.46) * mm});
            skLineSegment(sketch, "E335", {"start": v(123.5, 23.78) * mm, "end": v(125.7, 23.78) * mm});
            skLineSegment(sketch, "E336", {"start": v(123.5, 21.46) * mm, "end": v(125.7, 21.46) * mm});
            skArc(sketch, "E337", {"start": v(125.7, 21.46) * mm, "mid": v(126.42, 22.62) * mm, "end": v(125.7, 23.78) * mm});
            skArc(sketch, "E338", {"start": v(129.77, 23.73) * mm, "mid": v(129.08, 22.57) * mm, "end": v(129.77, 21.4) * mm});
            skLineSegment(sketch, "E339", {"start": v(129.77, 23.73) * mm, "end": v(131.97, 23.73) * mm});
            skLineSegment(sketch, "E340", {"start": v(129.77, 21.4) * mm, "end": v(131.97, 21.4) * mm});
            skArc(sketch, "E341", {"start": v(131.97, 21.4) * mm, "mid": v(132.7, 22.57) * mm, "end": v(131.97, 23.73) * mm});
            skArc(sketch, "E342", {"start": v(135.9, 23.67) * mm, "mid": v(135.22, 22.5) * mm, "end": v(135.9, 21.35) * mm});
            skLineSegment(sketch, "E343", {"start": v(135.9, 23.67) * mm, "end": v(138.1, 23.67) * mm});
            skLineSegment(sketch, "E344", {"start": v(135.9, 21.35) * mm, "end": v(138.1, 21.35) * mm});
            skArc(sketch, "E345", {"start": v(138.1, 21.35) * mm, "mid": v(138.83, 22.5) * mm, "end": v(138.1, 23.67) * mm});
            skArc(sketch, "E346", {"start": v(142.18, 23.62) * mm, "mid": v(141.5, 22.45) * mm, "end": v(142.18, 21.3) * mm});
            skLineSegment(sketch, "E347", {"start": v(142.18, 23.62) * mm, "end": v(144.38, 23.62) * mm});
            skLineSegment(sketch, "E348", {"start": v(142.18, 21.3) * mm, "end": v(144.38, 21.3) * mm});
            skArc(sketch, "E349", {"start": v(144.38, 21.3) * mm, "mid": v(145.1, 22.45) * mm, "end": v(144.38, 23.62) * mm});
            skArc(sketch, "E350", {"start": v(147.93, 23.84) * mm, "mid": v(147.23, 22.68) * mm, "end": v(147.93, 21.52) * mm});
            skLineSegment(sketch, "E351", {"start": v(147.93, 23.84) * mm, "end": v(150.12, 23.84) * mm});
            skLineSegment(sketch, "E352", {"start": v(147.93, 21.52) * mm, "end": v(150.12, 21.52) * mm});
            skArc(sketch, "E353", {"start": v(150.12, 21.52) * mm, "mid": v(150.85, 22.68) * mm, "end": v(150.12, 23.84) * mm});
            skArc(sketch, "E354", {"start": v(154.2, 23.78) * mm, "mid": v(153.51, 22.62) * mm, "end": v(154.2, 21.46) * mm});
            skLineSegment(sketch, "E355", {"start": v(154.2, 23.78) * mm, "end": v(156.4, 23.78) * mm});
            skLineSegment(sketch, "E356", {"start": v(154.2, 21.46) * mm, "end": v(156.4, 21.46) * mm});
            skArc(sketch, "E357", {"start": v(156.4, 21.46) * mm, "mid": v(157.13, 22.62) * mm, "end": v(156.4, 23.78) * mm});
            skArc(sketch, "E358", {"start": v(160.34, 23.73) * mm, "mid": v(159.65, 22.56) * mm, "end": v(160.34, 21.4) * mm});
            skLineSegment(sketch, "E359", {"start": v(160.34, 23.73) * mm, "end": v(162.53, 23.73) * mm});
            skLineSegment(sketch, "E360", {"start": v(160.34, 21.4) * mm, "end": v(162.53, 21.4) * mm});
            skArc(sketch, "E361", {"start": v(162.53, 21.4) * mm, "mid": v(163.26, 22.56) * mm, "end": v(162.53, 23.73) * mm});
            skSolve(sketch);
        }
        {
            var Q0;
            Q0=makeQuery(id+"F37.imprint","IMPRINT",FACE,{"disambiguationData":[TD([[makeQuery(id+"F37.imprint","IMPRINT",EDGE,{"derivedFrom":sQuery(id+"F37.wireOp",EDGE,"E302")}),1.0]])]});
            var Q1;
            {var subQ0=sQuery(id+"F37.wireOp",EDGE,"E307");Q1=makeQuery(id+"F37.imprint","IMPRINT",FACE,{"disambiguationData":[TD([[makeQuery(id+"F37.imprint","IMPRINT",EDGE,{"derivedFrom":subQ0}),-1.0]])]});}
            var Q2;
            {var subQ0=sQuery(id+"F37.wireOp",EDGE,"E311");Q2=makeQuery(id+"F37.imprint","IMPRINT",FACE,{"disambiguationData":[TD([[makeQuery(id+"F37.imprint","IMPRINT",EDGE,{"derivedFrom":subQ0}),-1.0]])]});}
            var Q3;
            {var subQ0=sQuery(id+"F37.wireOp",EDGE,"E315");Q3=makeQuery(id+"F37.imprint","IMPRINT",FACE,{"disambiguationData":[TD([[makeQuery(id+"F37.imprint","IMPRINT",EDGE,{"derivedFrom":subQ0}),-1.0]])]});}
            var Q4;
            {var subQ0=sQuery(id+"F37.wireOp",EDGE,"E319");Q4=makeQuery(id+"F37.imprint","IMPRINT",FACE,{"disambiguationData":[TD([[makeQuery(id+"F37.imprint","IMPRINT",EDGE,{"derivedFrom":subQ0}),-1.0]])]});}
            var Q5;
            {var subQ0=sQuery(id+"F37.wireOp",EDGE,"E323");Q5=makeQuery(id+"F37.imprint","IMPRINT",FACE,{"disambiguationData":[TD([[makeQuery(id+"F37.imprint","IMPRINT",EDGE,{"derivedFrom":subQ0}),-1.0]])]});}
            var Q6;
            {var subQ0=sQuery(id+"F37.wireOp",EDGE,"E327");Q6=makeQuery(id+"F37.imprint","IMPRINT",FACE,{"disambiguationData":[TD([[makeQuery(id+"F37.imprint","IMPRINT",EDGE,{"derivedFrom":subQ0}),-1.0]])]});}
            var Q7;
            {var subQ0=sQuery(id+"F37.wireOp",EDGE,"E331");Q7=makeQuery(id+"F37.imprint","IMPRINT",FACE,{"disambiguationData":[TD([[makeQuery(id+"F37.imprint","IMPRINT",EDGE,{"derivedFrom":subQ0}),-1.0]])]});}
            var Q8;
            {var subQ0=sQuery(id+"F37.wireOp",EDGE,"E335");Q8=makeQuery(id+"F37.imprint","IMPRINT",FACE,{"disambiguationData":[TD([[makeQuery(id+"F37.imprint","IMPRINT",EDGE,{"derivedFrom":subQ0}),-1.0]])]});}
            var Q9;
            {var subQ0=sQuery(id+"F37.wireOp",EDGE,"E339");Q9=makeQuery(id+"F37.imprint","IMPRINT",FACE,{"disambiguationData":[TD([[makeQuery(id+"F37.imprint","IMPRINT",EDGE,{"derivedFrom":subQ0}),-1.0]])]});}
            var Q10;
            {var subQ0=sQuery(id+"F37.wireOp",EDGE,"E343");Q10=makeQuery(id+"F37.imprint","IMPRINT",FACE,{"disambiguationData":[TD([[makeQuery(id+"F37.imprint","IMPRINT",EDGE,{"derivedFrom":subQ0}),-1.0]])]});}
            var Q11;
            {var subQ0=sQuery(id+"F37.wireOp",EDGE,"E347");Q11=makeQuery(id+"F37.imprint","IMPRINT",FACE,{"disambiguationData":[TD([[makeQuery(id+"F37.imprint","IMPRINT",EDGE,{"derivedFrom":subQ0}),-1.0]])]});}
            var Q12;
            {var subQ0=sQuery(id+"F37.wireOp",EDGE,"E351");Q12=makeQuery(id+"F37.imprint","IMPRINT",FACE,{"disambiguationData":[TD([[makeQuery(id+"F37.imprint","IMPRINT",EDGE,{"derivedFrom":subQ0}),-1.0]])]});}
            var Q13;
            {var subQ0=sQuery(id+"F37.wireOp",EDGE,"E355");Q13=makeQuery(id+"F37.imprint","IMPRINT",FACE,{"disambiguationData":[TD([[makeQuery(id+"F37.imprint","IMPRINT",EDGE,{"derivedFrom":subQ0}),-1.0]])]});}
            var Q14;
            {var subQ0=sQuery(id+"F37.wireOp",EDGE,"E359");Q14=makeQuery(id+"F37.imprint","IMPRINT",FACE,{"disambiguationData":[TD([[makeQuery(id+"F37.imprint","IMPRINT",EDGE,{"derivedFrom":subQ0}),-1.0]])]});}
            extrude(context, id + "F38", {"entities" : qUnion([Q0, Q1, Q2, Q3, Q4, Q5, Q6, Q7, Q8, Q9, Q10, Q11, Q12, Q13, Q14]), "operationType" : NewBodyOperationType.REMOVE, "oppositeDirection" : true, "depth" : 12.7 * mm, "offsetDistance" : 25.4 * mm});
        }
        {
            var Q0;
            {var subQ0=sQuery(id+"F28.wireOp",EDGE,"E90");Q0=makeQuery(id+"F30.boolean.opBoolean","MERGE",FACE,{"derivedFrom":[makeQuery(id+"F29.boolean.opBoolean","MERGE",FACE,{"derivedFrom":[makeQuery(id+"F1.opRevolve","SWEPT_FACE",FACE,{"disambiguationData":[OSD([sQuery(id+"F0.wireOp",EDGE,"E46")])]}),makeQuery(id+"F29.opExtrude","SWEPT_FACE",FACE,{"disambiguationData":[OSD([subQ0])]})]}),makeQuery(id+"F30.opExtrude","SWEPT_FACE",FACE,{"disambiguationData":[OSD([subQ0])]})]});}
            var sketch = newSketch(context, id + "F39", { "sketchPlane" : qUnion([Q0])});
            skCircle(sketch, "E362", {"center": v(0, 25.65) * mm, "radius": 3.17 * mm});
            skLineSegment(sketch, "E363", {"start": v(-2.08, 28.04) * mm, "end": v(2.08, 28.04) * mm});
            skLineSegment(sketch, "E364", {"start": v(2.98, 26.71) * mm, "end": v(2.08, 23.26) * mm});
            skLineSegment(sketch, "E365", {"start": v(-2.98, 26.71) * mm, "end": v(-2.08, 23.26) * mm});
            skSolve(sketch);
        }
        {
            var Q0;
            Q0 = qSketchRegion(id + "F39", true);
            extrude(context, id + "F40", {"entities" : qUnion([Q0]), "operationType" : NewBodyOperationType.ADD, "endBound" : BoundingType.SYMMETRIC, "depth" : 254 * mm, "offsetDistance" : 25.4 * mm});
        }
        {
            var Q0;
            Q0=makeQuery(id+"F33.opRevolve","SWEPT_FACE",FACE,{"disambiguationData":[OSD([sQuery(id+"F32.wireOp",EDGE,"E295")])]});
            var sketch = newSketch(context, id + "F41", { "sketchPlane" : qUnion([Q0])});
            skCircle(sketch, "E366", {"center": v(0, 36.79) * mm, "radius": 3.95 * mm});
            skSolve(sketch);
        }
        {
            var Q0;
            Q0 = qSketchRegion(id + "F41", true);
            extrude(context, id + "F42", {"entities" : qUnion([Q0]), "operationType" : NewBodyOperationType.REMOVE, "oppositeDirection" : true, "depth" : 2.3 * mm, "offsetDistance" : 25.4 * mm});
        }
        {
            var Q0;
            Q0=makeQuery(id+"F33.opRevolve","SWEPT_FACE",FACE,{"disambiguationData":[OSD([sQuery(id+"F32.wireOp",EDGE,"E292"),sQuery(id+"F32.wireOp",EDGE,"E298")])]});
            var sketch = newSketch(context, id + "F43", { "sketchPlane" : qUnion([Q0])});
            skCircle(sketch, "E367", {"center": v(0, 36.79) * mm, "radius": 3.05 * mm});
            skSolve(sketch);
        }
        {
            var Q0;
            Q0 = qSketchRegion(id + "F43", true);
            extrude(context, id + "F44", {"entities" : qUnion([Q0]), "operationType" : NewBodyOperationType.REMOVE, "oppositeDirection" : true, "depth" : 2.3 * mm, "offsetDistance" : 25.4 * mm});
        }
        {
            var Q0;
            {var subQ0=sQuery(id+"F39.wireOp",EDGE,"E363");Q0=makeQuery(id+"F39.imprint","IMPRINT",FACE,{"disambiguationData":[TD([[makeQuery(id+"F39.imprint","IMPRINT",EDGE,{"derivedFrom":subQ0}),1.0]])]});}
            var Q1;
            {var subQ0=sQuery(id+"F39.wireOp",EDGE,"E364");Q1=makeQuery(id+"F39.imprint","IMPRINT",FACE,{"disambiguationData":[TD([[makeQuery(id+"F39.imprint","IMPRINT",EDGE,{"derivedFrom":subQ0}),1.0]])]});}
            var Q2;
            {var subQ0=sQuery(id+"F39.wireOp",EDGE,"E365");Q2=makeQuery(id+"F39.imprint","IMPRINT",FACE,{"disambiguationData":[TD([[makeQuery(id+"F39.imprint","IMPRINT",EDGE,{"derivedFrom":subQ0}),-1.0]])]});}
            extrude(context, id + "F45", {"entities" : qUnion([Q0, Q1, Q2]), "operationType" : NewBodyOperationType.REMOVE, "depth" : 127 * mm, "offsetDistance" : 25.4 * mm});
        }
        {
            var Q0;
            Q0=makeQuery(id+"F40.opExtrude","CAP_FACE",FACE,{"disambiguationData":[OSD([sQuery(id+"F39.wireOp",EDGE,"E362")])],"isStart":false});
            var sketch = newSketch(context, id + "F46", { "sketchPlane" : qUnion([Q0])});
            skLineSegment(sketch, "E368", {"start": v(-5.9, 28.04) * mm, "end": v(-5.9, 22.84) * mm});
            skLineSegment(sketch, "E369", {"start": v(-5.9, 22.84) * mm, "end": v(5.9, 22.84) * mm});
            skLineSegment(sketch, "E370", {"start": v(5.9, 22.84) * mm, "end": v(5.9, 28.04) * mm});
            skLineSegment(sketch, "E371", {"start": v(-5.9, 28.04) * mm, "end": v(-5.9, 28.7) * mm});
            skLineSegment(sketch, "E372", {"start": v(-5.9, 28.7) * mm, "end": v(5.9, 28.7) * mm});
            skLineSegment(sketch, "E373", {"start": v(5.9, 28.7) * mm, "end": v(5.9, 28.04) * mm});
            skSolve(sketch);
        }
        {
            var Q0;
            Q0 = qSketchRegion(id + "F46", true);
            extrude(context, id + "F47", {"entities" : qUnion([Q0]), "operationType" : NewBodyOperationType.ADD, "depth" : 20.32 * mm, "offsetDistance" : 25.4 * mm});
        }
        {
            var Q0;
            Q0=makeQuery(id+"F47.opExtrude","SWEPT_FACE",FACE,{"disambiguationData":[OSD([sQuery(id+"F46.wireOp",EDGE,"E369")])]});
            extrude(context, id + "F48", {"entities" : qUnion([Q0]), "operationType" : NewBodyOperationType.ADD, "depth" : 2.03 * mm, "offsetDistance" : 25.4 * mm});
        }
        {
            var Q0;
            {var subQ0=sQuery(id+"F46.wireOp",EDGE,"E369");var subQ1=sQuery(id+"F46.wireOp",EDGE,"E368");Q0=makeQuery(id+"F48.boolean.opBoolean","MERGE",EDGE,{"derivedFrom":[makeQuery(id+"F47.opExtrude","CAP_EDGE",EDGE,{"disambiguationData":[OSD([subQ1,sQuery(id+"F46.wireOp",EDGE,"E371")])],"isStart":false}),makeQuery(id+"F48.opExtrude","SWEPT_EDGE",EDGE,{"disambiguationData":[OSD([subQ1,subQ0]),TDD([makeQuery(id+"F47.opExtrude","CAP_VERTEX",VERTEX,{"disambiguationData":[OSD([subQ1,subQ0])],"isStart":false})])]})]});}
            var Q1;
            {var subQ0=sQuery(id+"F46.wireOp",EDGE,"E370");var subQ1=sQuery(id+"F46.wireOp",EDGE,"E369");Q1=makeQuery(id+"F48.boolean.opBoolean","MERGE",EDGE,{"derivedFrom":[makeQuery(id+"F47.opExtrude","CAP_EDGE",EDGE,{"disambiguationData":[OSD([subQ0,sQuery(id+"F46.wireOp",EDGE,"E373")])],"isStart":false}),makeQuery(id+"F48.opExtrude","SWEPT_EDGE",EDGE,{"disambiguationData":[OSD([subQ1,subQ0]),TDD([makeQuery(id+"F47.opExtrude","CAP_VERTEX",VERTEX,{"disambiguationData":[OSD([subQ1,subQ0])],"isStart":false})])]})]});}
            chamfer(context, id + "F49", {"entities" : qUnion([Q0, Q1]), "width" : 4.32 * mm, "tangentPropagation" : true});
        }
        {
            var Q0;
            {var subQ0=sQuery(id+"F46.wireOp",EDGE,"E369");Q0=makeQuery(id+"F48.boolean.opBoolean","MERGE",FACE,{"derivedFrom":[makeQuery(id+"F47.opExtrude","CAP_FACE",FACE,{"disambiguationData":[OSD([sQuery(id+"F46.wireOp",EDGE,"E368"),subQ0,sQuery(id+"F46.wireOp",EDGE,"E370"),sQuery(id+"F46.wireOp",EDGE,"E371"),sQuery(id+"F46.wireOp",EDGE,"E372"),sQuery(id+"F46.wireOp",EDGE,"E373")])],"isStart":false}),makeQuery(id+"F48.opExtrude","SWEPT_FACE",FACE,{"disambiguationData":[OSD([subQ0]),TDD([makeQuery(id+"F47.opExtrude","CAP_EDGE",EDGE,{"disambiguationData":[OSD([subQ0])],"isStart":false})])]})]});}
            var sketch = newSketch(context, id + "F50", { "sketchPlane" : qUnion([Q0])});
            skCircle(sketch, "E374", {"center": v(0, 26.2) * mm, "radius": 2.05 * mm});
            skSolve(sketch);
        }
        {
            var Q0;
            Q0 = qSketchRegion(id + "F50", true);
            extrude(context, id + "F51", {"entities" : qUnion([Q0]), "operationType" : NewBodyOperationType.REMOVE, "oppositeDirection" : true, "depth" : 12.7 * mm, "offsetDistance" : 25.4 * mm});
        }
        {
            var Q0;
            {var subQ0=sQuery(id+"F46.wireOp",EDGE,"E368");Q0=makeQuery(id+"F48.boolean.opBoolean","MERGE",FACE,{"derivedFrom":[makeQuery(id+"F47.opExtrude","SWEPT_FACE",FACE,{"disambiguationData":[OSD([subQ0,sQuery(id+"F46.wireOp",EDGE,"E371")])]}),makeQuery(id+"F48.opExtrude","SWEPT_FACE",FACE,{"disambiguationData":[OSD([subQ0,sQuery(id+"F46.wireOp",EDGE,"E369")])]})]});}
            var sketch = newSketch(context, id + "F52", { "sketchPlane" : qUnion([Q0])});
            skLineSegment(sketch, "E375", {"start": v(297.06, 27.23) * mm, "end": v(297.06, 21.78) * mm});
            skLineSegment(sketch, "E376", {"start": v(297.06, 21.78) * mm, "end": v(300.15, 21.78) * mm});
            skLineSegment(sketch, "E377", {"start": v(300.15, 21.78) * mm, "end": v(300.15, 27.23) * mm});
            skLineSegment(sketch, "E378", {"start": v(300.15, 27.23) * mm, "end": v(297.06, 27.23) * mm});
            skLineSegment(sketch, "E379", {"start": v(302.89, 27.23) * mm, "end": v(302.89, 21.78) * mm});
            skLineSegment(sketch, "E380", {"start": v(302.89, 21.78) * mm, "end": v(305.97, 21.78) * mm});
            skLineSegment(sketch, "E381", {"start": v(305.97, 21.78) * mm, "end": v(305.97, 27.23) * mm});
            skLineSegment(sketch, "E382", {"start": v(305.97, 27.23) * mm, "end": v(302.89, 27.23) * mm});
            skSolve(sketch);
        }
        {
            var Q0;
            Q0 = qSketchRegion(id + "F52", true);
            extrude(context, id + "F53", {"entities" : qUnion([Q0]), "operationType" : NewBodyOperationType.REMOVE, "oppositeDirection" : true, "depth" : 3.8 * mm, "offsetDistance" : 25.4 * mm});
        }
        {
            var Q0;
            {var subQ0=sQuery(id+"F46.wireOp",EDGE,"E370");Q0=makeQuery(id+"F48.boolean.opBoolean","MERGE",FACE,{"derivedFrom":[makeQuery(id+"F47.opExtrude","SWEPT_FACE",FACE,{"disambiguationData":[OSD([subQ0,sQuery(id+"F46.wireOp",EDGE,"E373")])]}),makeQuery(id+"F48.opExtrude","SWEPT_FACE",FACE,{"disambiguationData":[OSD([sQuery(id+"F46.wireOp",EDGE,"E369"),subQ0])]})]});}
            var sketch = newSketch(context, id + "F54", { "sketchPlane" : qUnion([Q0])});
            skLineSegment(sketch, "E383", {"start": v(-305.8, 27.6) * mm, "end": v(-305.8, 22.15) * mm});
            skLineSegment(sketch, "E384", {"start": v(-305.8, 22.15) * mm, "end": v(-302.72, 22.15) * mm});
            skLineSegment(sketch, "E385", {"start": v(-302.72, 22.15) * mm, "end": v(-302.72, 27.6) * mm});
            skLineSegment(sketch, "E386", {"start": v(-302.72, 27.6) * mm, "end": v(-305.8, 27.6) * mm});
            skLineSegment(sketch, "E387", {"start": v(-299.98, 27.6) * mm, "end": v(-299.98, 22.15) * mm});
            skLineSegment(sketch, "E388", {"start": v(-299.98, 22.15) * mm, "end": v(-296.89, 22.15) * mm});
            skLineSegment(sketch, "E389", {"start": v(-296.89, 22.15) * mm, "end": v(-296.89, 27.6) * mm});
            skLineSegment(sketch, "E390", {"start": v(-296.89, 27.6) * mm, "end": v(-299.98, 27.6) * mm});
            skSolve(sketch);
        }
        {
            var Q0;
            Q0 = qSketchRegion(id + "F54", true);
            extrude(context, id + "F55", {"entities" : qUnion([Q0]), "operationType" : NewBodyOperationType.REMOVE, "oppositeDirection" : true, "depth" : 3.8 * mm, "offsetDistance" : 25.4 * mm});
        }
        {
            var Q0;
            Q0=makeQuery(id+"F10.opExtrude","CAP_FACE",FACE,{"disambiguationData":[OSD([sQuery(id+"F0.wireOp",EDGE,"E29"),sQuery(id+"F0.wireOp",EDGE,"E32"),sQuery(id+"F0.wireOp",EDGE,"E34"),sQuery(id+"F0.wireOp",EDGE,"E35")])],"isStart":false});
            var sketch = newSketch(context, id + "F56", { "sketchPlane" : qUnion([Q0])});
            skArc(sketch, "E391", {"start": v(-4.59, 10.68) * mm, "mid": v(-3.97, 6.58) * mm, "end": v(-0.8, 3.9) * mm});
            skArc(sketch, "E392", {"start": v(-5.54, 10.67) * mm, "mid": v(-4.88, 6.3) * mm, "end": v(-1.55, 3.38) * mm});
            skLineSegment(sketch, "E393", {"start": v(-1.55, 3.38) * mm, "end": v(-0.8, 3.9) * mm});
            skLineSegment(sketch, "E394", {"start": v(-4.59, 10.68) * mm, "end": v(-5.54, 10.67) * mm});
            skSolve(sketch);
        }
        {
            var Q0;
            Q0 = qSketchRegion(id + "F56", true);
            extrude(context, id + "F57", {"entities" : qUnion([Q0]), "operationType" : NewBodyOperationType.ADD, "oppositeDirection" : true, "depth" : 0.76 * mm, "offsetDistance" : 25.4 * mm});
        }
    });
